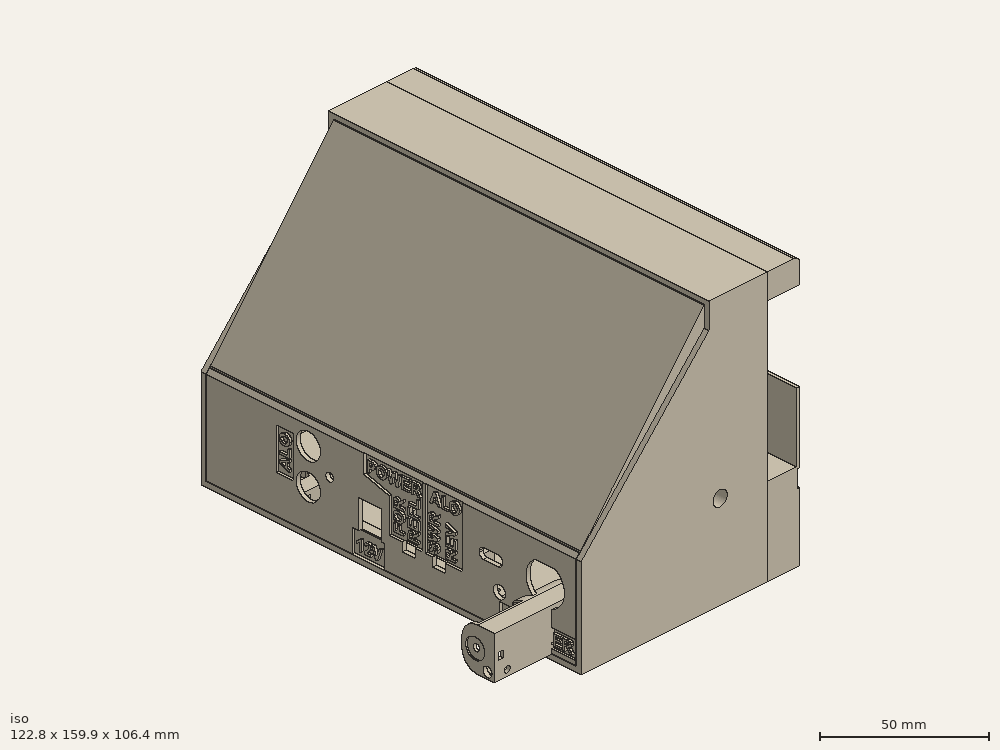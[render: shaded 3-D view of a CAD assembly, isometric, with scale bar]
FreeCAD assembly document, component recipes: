
FREECAD ASSEMBLY — COMPONENT RECIPES ("console")

This assembly document has 6 components, labeled P0..P5 below (a component is one placed body or linked part). 5 of them carry a construction recipe — the FreeCAD feature program that regenerates the part from scratch, quoted from this document or its linked companion documents; the rest are supplied as boundary geometry only. No exploded tour is included for this assembly.
NOTE — this tour is split across 2 documents so each fits a 32k-token context. This is document 1: the component sections continue in the remaining 1 document, each repeating the header above.
COMPONENT P0 — geometry summary ("AA single002"; no construction recipe available for this part):
  bounding box: 122.8 x 16.9 x 13.9 mm
  tessellated surface: 93,791 triangles
  volume: 2869 mm^3 (10% of its bounding box)
COMPONENT P1 — recipe-attached ("Cliff FC684204", modeled in this document).
Construction recipe (the document's own serialized feature program — sketch geometry with constraints, then the solid features built on it; lengths are millimeters unless a unit is written):

FEATURE [PartDesign::SubShapeBinder] Binder
  BindCopyOnChange = 0
  BindMode = 0
  ClaimChildren = false
  Context = -> Part [Body.Binder.]
  Fuse = false
  MakeFace = true
  OffsetFill = false
  OffsetIntersection = false
  OffsetJoinType = 0
  OffsetOpenResult = false
  PartialLoad = false
  Refine = true
  Relative = true
  Support = -> [<external console-placement.FCStd>#Assembly[meter.,meter001.,_M_pot.,_00DP6R7BLKM3QEBLK003.]]
  _Version = 2
FEATURE [PartDesign::SubShapeBinder] Binder001
  BindCopyOnChange = 0
  BindMode = 0
  ClaimChildren = false
  Context = -> Part [Body.Binder001.]
  Fuse = false
  MakeFace = true
  OffsetFill = false
  OffsetIntersection = false
  OffsetJoinType = 0
  OffsetOpenResult = false
  PartialLoad = false
  Refine = true
  Relative = true
  Support = -> [<external console-placement.FCStd>#Assembly[PCB_Assembly.pcb_imported.]]
  _Version = 2
FEATURE [PartDesign::Plane] DatumPlane  label="meter back"
  AttachmentSupport = -> [Binder]
  Length = 190.224
  MapMode = 5
  Placement = pos=(76.55,0,0) rot=(0.57735,-0.57735,-0.57735;2.0944rad)
  ResizeMode = 0
  Width = 149.914
FEATURE [Sketcher::SketchObject] Sketch
  ArcFitTolerance = 1e-06
  AttachmentSupport = -> [Binder]
  ExternalGeometry = -> [Binder,Binder001]
  FullyConstrained = true
  MakeInternals = false
  MapMode = 5
  Placement = pos=(76.55,0,0) rot=(0.57735,-0.57735,-0.57735;2.0944rad)
  sketch-geometry (17):
    g0: LineSegment StartX=-137.1 StartY=86.63 StartZ=0 EndX=-137.1 EndY=-7.62 EndZ=0
    g1: LineSegment StartX=-137.1 StartY=-7.62 StartZ=0 EndX=22.8 EndY=-7.62 EndZ=0
    g2: LineSegment StartX=22.8 StartY=-7.62 StartZ=0 EndX=22.8 EndY=86.63 EndZ=0
    g3: LineSegment [constr] StartX=22.8 StartY=86.63 StartZ=0 EndX=-137.1 EndY=86.63 EndZ=0
    g4: Circle CenterX=-125.984 CenterY=80.264 CenterZ=0 NormalX=0 NormalY=0 NormalZ=1 AngleXU=0 Radius=1.905
    g5: Circle CenterX=-77.216 CenterY=80.264 CenterZ=0 NormalX=0 NormalY=0 NormalZ=1 AngleXU=0 Radius=1.905
    g6: Circle CenterX=-125.984 CenterY=31.496 CenterZ=0 NormalX=0 NormalY=0 NormalZ=1 AngleXU=0 Radius=1.905
    g7: Circle CenterX=-77.216 CenterY=31.496 CenterZ=0 NormalX=0 NormalY=0 NormalZ=1 AngleXU=0 Radius=1.905
    g8: Circle CenterX=-101.6 CenterY=55.88 CenterZ=0 NormalX=0 NormalY=0 NormalZ=1 AngleXU=0 Radius=27.178
    g9: Circle CenterX=-12.7 CenterY=55.88 CenterZ=0 NormalX=0 NormalY=0 NormalZ=1 AngleXU=0 Radius=27.178
    g10: Circle CenterX=-37.084 CenterY=31.496 CenterZ=0 NormalX=0 NormalY=0 NormalZ=1 AngleXU=0 Radius=1.905
    g11: Circle CenterX=11.684 CenterY=31.496 CenterZ=0 NormalX=0 NormalY=0 NormalZ=1 AngleXU=0 Radius=1.905
    g12: Circle CenterX=11.684 CenterY=80.264 CenterZ=0 NormalX=0 NormalY=0 NormalZ=1 AngleXU=0 Radius=1.905
    g13: Circle CenterX=-37.084 CenterY=80.264 CenterZ=0 NormalX=0 NormalY=0 NormalZ=1 AngleXU=0 Radius=1.905
    g14: LineSegment StartX=-137.1 StartY=86.63 StartZ=0 EndX=-137.1 EndY=96.79 EndZ=0
    g15: LineSegment StartX=-137.1 StartY=96.79 StartZ=0 EndX=22.8 EndY=96.79 EndZ=0
    g16: LineSegment StartX=22.8 StartY=96.79 StartZ=0 EndX=22.8 EndY=86.63 EndZ=0
  constraints (38):
    c: Coincident(g0,g1)
    c: Coincident(g1,g2)
    c: Coincident(g2,g3)
    c: Coincident(g3,g0)
    c: Vertical(g0)
    c: Vertical(g2)
    c: Horizontal(g1)
    c: Coincident(g0,g-4)
    c: Coincident(g-3,g2)
    c: PointOnObject(g-18,g1)
    c: Coincident(g4,g-11)
    c: Coincident(g5,g-9)
    c: Coincident(g6,g-12)
    c: Coincident(g7,g-10)
    c: Coincident(g8,g-8)
    c: Coincident(g9,g-7)
    c: Coincident(g10,g-13)
    c: Coincident(g11,g-16)
    c: Coincident(g12,g-15)
    c: Coincident(g13,g-14)
    c: Equal(g4,g5)
    c: Equal(g4,g6)
    c: Equal(g4,g7)
    c: Equal(g4,g13)
    c: Equal(g4,g12)
    c: Equal(g4,g10)
    c: Equal(g4,g11)
    c: Equal(g8,g9)
    c: Diameter(g8) = 54.356
    c: Diameter(g4) = 3.81
    c: Coincident(g14,g0)
    c: Vertical(g14)
    c: Coincident(g15,g14)
    c: Horizontal(g15)
    c: Coincident(g16,g15)
    c: Coincident(g16,g2)
    c: Vertical(g16)
    c: DistanceY(g2,g15) = 10.16
FEATURE [PartDesign::Pad] Pad
  Direction = (-1,0,0)
  Length = 2.032
  Length2 = 10
  Profile = -> Sketch
  ReferenceAxis = -> Sketch [N_Axis]
  Refine = true
  Suppressed = false
  Type = 0
FEATURE [Sketcher::SketchObject] Sketch001
  ArcFitTolerance = 1e-06
  AttachmentSupport = -> [DatumPlane]
  ExternalGeometry = -> [Pad]
  FullyConstrained = false
  MakeInternals = false
  MapMode = 5
  Placement = pos=(76.55,0,0) rot=(0.57735,-0.57735,-0.57735;2.0944rad)
  sketch-geometry (11):
    g0: LineSegment StartX=-137.1 StartY=96.79 StartZ=0 EndX=-137.1 EndY=-9.652 EndZ=0
    g1: LineSegment StartX=-137.1 StartY=-9.652 StartZ=0 EndX=22.8 EndY=-9.652 EndZ=0
    g2: LineSegment StartX=22.8 StartY=-9.652 StartZ=0 EndX=22.8 EndY=96.79 EndZ=0
    g3: LineSegment StartX=-135.068 StartY=94.758 StartZ=0 EndX=-135.068 EndY=-7.62 EndZ=0
    g4: LineSegment StartX=-135.068 StartY=-7.62 StartZ=0 EndX=20.768 EndY=-7.62 EndZ=0
    g5: LineSegment StartX=20.768 StartY=-7.62 StartZ=0 EndX=20.768 EndY=94.758 EndZ=0
    g6: LineSegment StartX=-137.1 StartY=96.79 StartZ=0 EndX=22.8 EndY=96.79 EndZ=0
    g7: LineSegment StartX=20.768 StartY=94.758 StartZ=0 EndX=-135.068 EndY=94.758 EndZ=0
    g8: LineSegment [constr] StartX=-57.15 StartY=94.758 StartZ=0 EndX=-57.15 EndY=96.79 EndZ=0
    g9: LineSegment [constr] StartX=-57.15 StartY=-7.62 StartZ=0 EndX=-57.15 EndY=-9.652 EndZ=0
    g10: LineSegment [constr] StartX=-135.068 StartY=46.1442 StartZ=0 EndX=-137.1 EndY=46.1442 EndZ=0
  constraints (29):
    c: Coincident(g0,g1)
    c: Coincident(g1,g2)
    c: Vertical(g0)
    c: Vertical(g2)
    c: Horizontal(g1)
    c: DistanceY(g1,g-3) = 2.032
    c: Coincident(g3,g4)
    c: Coincident(g4,g5)
    c: Vertical(g3)
    c: Vertical(g5)
    c: Horizontal(g4)
    c: PointOnObject(g-3,g4)
    c: Coincident(g2,g-4)
    c: Coincident(g0,g-4)
    c: Coincident(g6,g0)
    c: Coincident(g6,g2)
    c: Coincident(g7,g5)
    c: Coincident(g7,g3)
    c: Horizontal(g7)
    c: Symmetric(g7,g7,g8)
    c: Symmetric(g6,g6,g8)
    c: Vertical(g8)
    c: Symmetric(g4,g4,g9)
    c: Symmetric(g1,g1,g9)
    c: Equal(g9,g8)
    c: PointOnObject(g10,g3)
    c: PointOnObject(g10,g0)
    c: Horizontal(g10)
    c: Equal(g10,g8)
FEATURE [PartDesign::Pad] Pad001
  BaseFeature = -> Pad
  Direction = (-1,0,0)
  Length = 10
  Length2 = 10
  Profile = -> Sketch001
  ReferenceAxis = -> Sketch001 [N_Axis]
  Refine = true
  Suppressed = false
  Type = 3
  UpToFace = -> Binder001 [Face2]
FEATURE [PartDesign::Plane] DatumPlane001  label="console left"
  AttachmentSupport = -> [Binder]
  Length = 123.815
  MapMode = 5
  Placement = pos=(0,137.1,1.51e-14) rot=(0,0.707107,0.707107;3.14159rad)
  ResizeMode = 0
  Width = 144.055
FEATURE [Sketcher::SketchObject] Sketch002  label="angled back sketch"
  ArcFitTolerance = 1e-06
  AttachmentSupport = -> [DatumPlane001]
  ExternalGeometry = -> [Binder,Pad001]
  FullyConstrained = false
  MakeInternals = false
  MapMode = 5
  Placement = pos=(0,137.1,1.51e-14) rot=(0,0.707107,0.707107;3.14159rad)
  sketch-geometry (5):
    g0: LineSegment StartX=-52.039 StartY=86.63 StartZ=0 EndX=0 EndY=30.988 EndZ=0
    g1: LineSegment StartX=-52.039 StartY=86.63 StartZ=0 EndX=-52.039 EndY=104.011 EndZ=0
    g2: LineSegment StartX=-52.039 StartY=104.011 StartZ=0 EndX=12.4998 EndY=104.011 EndZ=0
    g3: LineSegment StartX=12.4998 StartY=104.011 StartZ=0 EndX=12.4998 EndY=30.988 EndZ=0
    g4: LineSegment StartX=12.4998 StartY=30.988 StartZ=0 EndX=0 EndY=30.988 EndZ=0
  constraints (13):
    c: PointOnObject(g0,g-3)
    c: Vertical(g0,g-5)
    c: DistanceY(g-5,g0) = 40.64
    c: PointOnObject(g0,g-4)
    c: Coincident(g1,g0)
    c: Vertical(g1)
    c: Coincident(g2,g1)
    c: Horizontal(g2)
    c: Coincident(g3,g2)
    c: Vertical(g3)
    c: Coincident(g4,g3)
    c: Coincident(g4,g0)
    c: Horizontal(g4)
FEATURE [PartDesign::Pocket] Pocket
  BaseFeature = -> Pad001
  Direction = (0,-1,2e-16)
  Length = 5
  Length2 = 5
  Profile = -> Sketch002
  ReferenceAxis = -> Sketch002 [N_Axis]
  Refine = true
  Suppressed = false
  Type = 1
FEATURE [PartDesign::SubShapeBinder] Binder003
  BindCopyOnChange = 0
  BindMode = 0
  ClaimChildren = false
  Context = -> Part [Body.Binder003.]
  Fuse = false
  MakeFace = true
  OffsetFill = false
  OffsetIntersection = false
  OffsetJoinType = 0
  OffsetOpenResult = false
  PartialLoad = false
  Refine = true
  Relative = true
  Support = -> [Link[PCB_Assembly.WP154A4SUREQBFZGC.,PCB_Assembly.WP154A4SUREQBFZGC001.,PCB_Assembly.WP154A4SUREQBFZGC002.,PCB_Assembly.WP154A4SUREQBFZGC003.,PCB_Assembly.WP154A4SUREQBFZGC004.,PCB_Assembly.WP154A4SUREQBFZGC005.,_M_pot.,_00DP6R7BLKM3QEBLK003.]]
  _Version = 2
FEATURE [Sketcher::SketchObject] Sketch025
  ArcFitTolerance = 1e-06
  AttachmentSupport = -> [DatumPlane]
  ExternalGeometry = -> [Binder]
  FullyConstrained = true
  MakeInternals = false
  MapMode = 5
  Placement = pos=(76.55,0,0) rot=(0.57735,-0.57735,-0.57735;2.0944rad)
  sketch-geometry (15):
    g0: Circle [constr] CenterX=-131.385 CenterY=91.075 CenterZ=0 NormalX=0 NormalY=0 NormalZ=1 AngleXU=0 Radius=3.683
    g1: Circle CenterX=-131.385 CenterY=91.075 CenterZ=0 NormalX=0 NormalY=0 NormalZ=1 AngleXU=0 Radius=1.524
    g2: Circle [constr] CenterX=17.085 CenterY=91.075 CenterZ=0 NormalX=0 NormalY=0 NormalZ=1 AngleXU=0 Radius=3.683
    g3: Circle CenterX=17.085 CenterY=91.075 CenterZ=0 NormalX=0 NormalY=0 NormalZ=1 AngleXU=0 Radius=1.524
    g4: Circle [constr] CenterX=-109.668 CenterY=-3.937 CenterZ=0 NormalX=0 NormalY=0 NormalZ=1 AngleXU=0 Radius=3.683
    g5: Circle [constr] CenterX=16.958 CenterY=-3.937 CenterZ=0 NormalX=0 NormalY=0 NormalZ=1 AngleXU=0 Radius=3.683
    g6: Circle CenterX=-109.668 CenterY=-3.937 CenterZ=0 NormalX=0 NormalY=0 NormalZ=1 AngleXU=0 Radius=1.524
    g7: Circle CenterX=16.958 CenterY=-3.937 CenterZ=0 NormalX=0 NormalY=0 NormalZ=1 AngleXU=0 Radius=1.524
    g8: LineSegment [constr] StartX=-66.1 StartY=86.63 StartZ=0 EndX=-48.2 EndY=25.13 EndZ=0
    g9: Circle CenterX=-57.15 CenterY=55.88 CenterZ=0 NormalX=0 NormalY=0 NormalZ=1 AngleXU=0 Radius=1.524
    g10: LineSegment StartX=-62.8269 StartY=92.98 StartZ=0 EndX=-62.8269 EndY=79.7415 EndZ=0
    g11: LineSegment StartX=-62.8269 StartY=79.7415 StartZ=0 EndX=-51.4731 EndY=79.7415 EndZ=0
    g12: LineSegment StartX=-51.4731 StartY=79.7415 StartZ=0 EndX=-51.4731 EndY=92.98 EndZ=0
    g13: LineSegment StartX=-51.4731 StartY=92.98 StartZ=0 EndX=-62.8269 EndY=92.98 EndZ=0
    g14: GeomPoint X=-57.15 Y=79.7415 Z=0
  constraints (37):
    c: Diameter(g0) = 7.366
    c: Tangent(g0,g-4)
    c: Tangent(g0,g-3)
    c: Coincident(g1,g0)
    c: Diameter(g1) = 3.048
    c: Equal(g2,g0)
    c: Tangent(g2,g-5)
    c: Tangent(g2,g-3)
    c: Coincident(g3,g2)
    c: Equal(g3,g1)
    c: Equal(g4,g5)
    c: Equal(g4,g0)
    c: Tangent(g4,g-6)
    c: Tangent(g5,g-6)
    c: DistanceX(g-6,g4) = 25.4
    c: DistanceX(g5,g-6) = 3.81
    c: Coincident(g6,g4)
    c: Coincident(g7,g5)
    c: Equal(g7,g6)
    c: Equal(g6,g1)
    c: Coincident(g8,g-7)
    c: Coincident(g8,g-8)
    c: Symmetric(g8,g8,g9)
    c: Equal(g9,g7)
    c: Coincident(g10,g11)
    c: Coincident(g11,g12)
    c: Coincident(g12,g13)
    c: Coincident(g13,g10)
    c: Vertical(g10)
    c: Vertical(g12)
    c: Horizontal(g11)
    c: Horizontal(g13)
    c: Symmetric(g11,g10,g14)
    c: Vertical(g9,g14)
    c: DistanceX(g10,g12) = 11.3538
    c: DistanceY(g11,g12) = 13.2385
    c: DistanceY(g12,g-5) = 1.778
FEATURE [PartDesign::Pocket] Pocket009  label="screw holes to front panel"
  BaseFeature = -> Pocket
  Direction = (1,0,0)
  Length = 5.00126
  Length2 = 5
  Profile = -> Sketch025
  ReferenceAxis = -> Sketch025 [N_Axis]
  Refine = true
  Reversed = true
  Suppressed = false
  Type = 1
FEATURE [PartDesign::Plane] DatumPlane004  label="normal to sloped lid"
  AttachmentSupport = -> [Pocket009]
  Length = 194.066
  MapMode = 7
  Placement = pos=(52.039,-20.768,86.63) rot=(0.344679,0.344679,0.873151;1.70603rad)
  ResizeMode = 0
  Width = 189.332
FEATURE [Sketcher::SketchObject] Sketch027
  ArcFitTolerance = 1e-06
  AttachmentSupport = -> [DatumPlane004]
  ExternalGeometry = -> [Pocket009]
  FullyConstrained = true
  MakeInternals = false
  MapMode = 5
  Placement = pos=(52.039,-20.768,86.63) rot=(0.344679,0.344679,0.873151;1.70603rad)
  sketch-geometry (6):
    g0: LineSegment StartX=0 StartY=-4.318 StartZ=0 EndX=2.54 EndY=-1.778 EndZ=0
    g1: LineSegment StartX=2.54 StartY=-1.778 StartZ=0 EndX=0 EndY=-1.778 EndZ=0
    g2: LineSegment StartX=0 StartY=-1.778 StartZ=0 EndX=0 EndY=-4.318 EndZ=0
    g3: LineSegment StartX=153.296 StartY=-1.778 StartZ=0 EndX=155.836 EndY=-1.778 EndZ=0
    g4: LineSegment StartX=155.836 StartY=-1.778 StartZ=0 EndX=155.836 EndY=-4.318 EndZ=0
    g5: LineSegment StartX=155.836 StartY=-4.318 StartZ=0 EndX=153.296 EndY=-1.778 EndZ=0
  constraints (18):
    c: Coincident(g1,g0)
    c: PointOnObject(g1,g-2)
    c: Horizontal(g1)
    c: Coincident(g2,g1)
    c: Vertical(g2)
    c: Coincident(g0,g2)
    c: DistanceY(g1,g-1) = 1.778
    c: Distance(g1,g1) = 2.54
    c: Angle(g0,g2) = 0.785398
    c: Horizontal(g3)
    c: Coincident(g4,g3)
    c: Vertical(g4)
    c: Coincident(g5,g4)
    c: Coincident(g5,g3)
    c: Vertical(g3,g-3)
    c: Horizontal(g3,g0)
    c: Equal(g1,g3)
    c: Equal(g5,g0)
FEATURE [PartDesign::Pad] Pad006  label="lid shelf"
  BaseFeature = -> Pocket009
  Direction = (0.683065,0,0.730358)
  Length = 10
  Length2 = 10
  Profile = -> Sketch027
  ReferenceAxis = -> Sketch027 [N_Axis]
  Refine = true
  Reversed = true
  Suppressed = false
  Type = 3
  UpToFace = -> Pocket009 [Face32]
FEATURE [PartDesign::Plane] DatumPlane005  label="PCB back"
  AttachmentSupport = -> [Binder001]
  Length = 190.224
  MapMode = 5
  Placement = pos=(0,0,0) rot=(0.57735,-0.57735,-0.57735;2.0944rad)
  ResizeMode = 0
  Width = 149.914
FEATURE [Sketcher::SketchObject] Sketch028
  ArcFitTolerance = 1e-06
  AttachmentSupport = -> [DatumPlane005]
  ExternalGeometry = -> [Pad006,DatumPlane001]
  FullyConstrained = false
  MakeInternals = false
  MapMode = 5
  Placement = pos=(0,0,0) rot=(0.57735,-0.57735,-0.57735;2.0944rad)
  sketch-geometry (8):
    g0: LineSegment StartX=-137.1 StartY=-9.652 StartZ=0 EndX=22.8 EndY=-9.652 EndZ=0
    g1: LineSegment StartX=22.8 StartY=-9.652 StartZ=0 EndX=22.8 EndY=30.988 EndZ=0
    g2: LineSegment StartX=22.8 StartY=30.988 StartZ=0 EndX=20.768 EndY=30.988 EndZ=0
    g3: LineSegment StartX=20.768 StartY=30.988 StartZ=0 EndX=20.768 EndY=-7.62 EndZ=0
    g4: LineSegment StartX=20.768 StartY=-7.62 StartZ=0 EndX=-135.068 EndY=-7.62 EndZ=0
    g5: LineSegment StartX=-135.068 StartY=-7.62 StartZ=0 EndX=-135.068 EndY=30.988 EndZ=0
    g6: LineSegment StartX=-137.1 StartY=30.988 StartZ=0 EndX=-137.1 EndY=-9.652 EndZ=0
    g7: LineSegment StartX=-135.068 StartY=30.988 StartZ=0 EndX=-137.1 EndY=30.988 EndZ=0
  constraints (14):
    c: Coincident(g0,g-4)
    c: Coincident(g1,g0)
    c: Coincident(g1,g-3)
    c: Coincident(g2,g1)
    c: Coincident(g2,g-6)
    c: Coincident(g3,g2)
    c: Coincident(g3,g-5)
    c: Coincident(g4,g3)
    c: Coincident(g4,g-5)
    c: Coincident(g5,g4)
    c: Coincident(g5,g-8)
    c: Coincident(g7,g5)
    c: Coincident(g7,g6)
    c: Horizontal(g7)
FEATURE [PartDesign::Pad] Pad007  label="extend back"
  BaseFeature = -> Pad006
  Direction = (-1,0,0)
  Length = 1.651
  Length2 = 10
  Profile = -> Sketch028
  ReferenceAxis = -> Sketch028 [N_Axis]
  Refine = true
  Suppressed = false
  Type = 0
FEATURE [PartDesign::Plane] DatumPlane006  label="sub panel bottom"
  AttachmentSupport = -> [Pad006]
  Length = 127.233
  MapMode = 5
  Placement = pos=(0,0,-9.652) rot=(1,0,0;3.14159rad)
  ResizeMode = 0
  Width = 187.783
FEATURE [Sketcher::SketchObject] Sketch029
  ArcFitTolerance = 1e-06
  AttachmentSupport = -> [DatumPlane006]
  ExternalGeometry = -> [Pad006]
  FullyConstrained = true
  MakeInternals = false
  MapMode = 5
  Placement = pos=(0,0,-9.652) rot=(1,0,0;3.14159rad)
  sketch-geometry (6):
    g0: LineSegment StartX=0 StartY=20.768 StartZ=0 EndX=0 EndY=18.228 EndZ=0
    g1: LineSegment StartX=0 StartY=18.228 StartZ=0 EndX=3.81 EndY=20.768 EndZ=0
    g2: LineSegment StartX=3.81 StartY=20.768 StartZ=0 EndX=0 EndY=20.768 EndZ=0
    g3: LineSegment StartX=0 StartY=-135.068 StartZ=0 EndX=0 EndY=-132.528 EndZ=0
    g4: LineSegment StartX=0 StartY=-135.068 StartZ=0 EndX=3.81 EndY=-135.068 EndZ=0
    g5: LineSegment StartX=3.81 StartY=-135.068 StartZ=0 EndX=0 EndY=-132.528 EndZ=0
  constraints (15):
    c: Coincident(g0,g-4)
    c: Coincident(g0,g-7)
    c: Coincident(g1,g0)
    c: Coincident(g2,g1)
    c: Coincident(g2,g0)
    c: Coincident(g3,g-5)
    c: Vertical(g3)
    c: Equal(g3,g0)
    c: Horizontal(g2)
    c: DistanceX(g0,g1) = 3.81
    c: Coincident(g4,g3)
    c: Coincident(g5,g4)
    c: Coincident(g5,g3)
    c: Horizontal(g4)
    c: Equal(g5,g1)
FEATURE [PartDesign::Pad] Pad008
  BaseFeature = -> Pad007
  Direction = (0,0,-1)
  Length = 27.94
  Length2 = 10
  Profile = -> Sketch029
  ReferenceAxis = -> Sketch029 [N_Axis]
  Refine = true
  Reversed = true
  Suppressed = false
  Type = 3
  UpToFace = -> Pad007 [Face37]
FEATURE [Sketcher::SketchObject] Sketch030
  ArcFitTolerance = 1e-06
  AttachmentSupport = -> [DatumPlane001]
  ExternalGeometry = -> [Pad008]
  FullyConstrained = true
  MakeInternals = false
  MapMode = 5
  Placement = pos=(0,137.1,1.51e-14) rot=(0,0.707107,0.707107;3.14159rad)
  sketch-geometry (3):
    g0: LineSegment StartX=-3.04e-14 StartY=-7.62 StartZ=0 EndX=-3.04e-14 EndY=-6.35 EndZ=0
    g1: LineSegment StartX=-3.04e-14 StartY=-6.35 StartZ=0 EndX=-1.27 EndY=-7.62 EndZ=0
    g2: LineSegment StartX=-1.27 StartY=-7.62 StartZ=0 EndX=-3.04e-14 EndY=-7.62 EndZ=0
  constraints (8):
    c: Coincident(g0,g-3)
    c: Coincident(g1,g0)
    c: Coincident(g2,g1)
    c: Coincident(g2,g0)
    c: Horizontal(g2)
    c: Vertical(g0)
    c: Angle(g2,g1) = 0.785398
    c: DistanceY(g0,g0) = 1.27
FEATURE [PartDesign::Pad] Pad009  label="back panel block"
  BaseFeature = -> Pad008
  Direction = (0,1,-2e-16)
  Length = 10
  Length2 = 10
  Profile = -> Sketch030
  ReferenceAxis = -> Sketch030 [N_Axis]
  Refine = true
  Suppressed = false
  Type = 3
  UpToFace = -> Pad008 [Face27]
FEATURE [PartDesign::Plane] DatumPlane011  label="PCB left (gapped)"
  AttachmentOffset = pos=(0,0,2.54) rot=(0,0,1;0rad)
  AttachmentSupport = -> [Binder001]
  Length = 123.815
  MapMode = 5
  Placement = pos=(0,104.14,-6e-16) rot=(0,0.707107,0.707107;3.14159rad)
  ResizeMode = 0
  Width = 144.055
FEATURE [PartDesign::Plane] DatumPlane012  label="PCB right (gapped)"
  AttachmentOffset = pos=(0,0,2.54) rot=(0,0,1;0rad)
  AttachmentSupport = -> [Binder001]
  Length = 123.815
  MapMode = 5
  Placement = pos=(0,-2.54,6e-16) rot=(1,0,0;1.5708rad)
  ResizeMode = 0
  Width = 144.055
FEATURE [Sketcher::SketchObject] Sketch038
  ArcFitTolerance = 1e-06
  AttachmentSupport = -> [DatumPlane011]
  ExternalGeometry = -> [Pad009]
  FullyConstrained = true
  MakeInternals = false
  MapMode = 5
  Placement = pos=(0,104.14,-6e-16) rot=(0,0.707107,0.707107;3.14159rad)
  sketch-geometry (4):
    g0: LineSegment StartX=-21.971 StartY=-9.652 StartZ=0 EndX=-17.399 EndY=-5.08 EndZ=0
    g1: LineSegment StartX=-17.399 StartY=-5.08 StartZ=0 EndX=-4.699 EndY=-5.08 EndZ=0
    g2: LineSegment StartX=-4.699 StartY=-5.08 StartZ=0 EndX=-4.699 EndY=-9.652 EndZ=0
    g3: LineSegment StartX=-4.699 StartY=-9.652 StartZ=0 EndX=-21.971 EndY=-9.652 EndZ=0
  constraints (12):
    c: PointOnObject(g0,g-3)
    c: Coincident(g1,g0)
    c: Horizontal(g1)
    c: Coincident(g2,g1)
    c: PointOnObject(g2,g-3)
    c: Vertical(g2)
    c: Coincident(g3,g2)
    c: Coincident(g3,g0)
    c: Angle(g3,g0) = 0.785398
    c: Distance(g2,g1) = 4.572
    c: DistanceX(g2,g-3) = 6.35
    c: DistanceX(g0,g1) = 12.7
FEATURE [PartDesign::Pad] Pad014  label="bottom boss"
  BaseFeature = -> Pad009
  Direction = (0,1,-2e-16)
  Length = 12.7
  Length2 = 10
  Profile = -> Sketch038
  ReferenceAxis = -> Sketch038 [N_Axis]
  Refine = true
  Suppressed = false
  Type = 0
FEATURE [Sketcher::SketchObject] Sketch039
  ArcFitTolerance = 1e-06
  AttachmentSupport = -> [DatumPlane012]
  ExternalGeometry = -> [Pad014]
  FullyConstrained = true
  MakeInternals = false
  MapMode = 5
  Placement = pos=(0,-2.54,6e-16) rot=(1,0,0;1.5708rad)
  sketch-geometry (4):
    g0: LineSegment StartX=4.699 StartY=-5.08 StartZ=0 EndX=17.399 EndY=-5.08 EndZ=0
    g1: LineSegment StartX=17.399 StartY=-5.08 StartZ=0 EndX=21.971 EndY=-9.652 EndZ=0
    g2: LineSegment StartX=21.971 StartY=-9.652 StartZ=0 EndX=4.699 EndY=-9.652 EndZ=0
    g3: LineSegment StartX=4.699 StartY=-9.652 StartZ=0 EndX=4.699 EndY=-5.08 EndZ=0
  constraints (10):
    c: Coincident(g0,g-4)
    c: Coincident(g0,g-5)
    c: Coincident(g1,g0)
    c: PointOnObject(g1,g-3)
    c: Coincident(g2,g1)
    c: PointOnObject(g2,g-3)
    c: Coincident(g3,g2)
    c: Coincident(g3,g0)
    c: Vertical(g3)
    c: PointOnObject(g-5,g1)
FEATURE [PartDesign::Pad] Pad015  label="bottom boss 2"
  BaseFeature = -> Pad014
  Direction = (0,-1,2e-16)
  Length = 12.7
  Length2 = 10
  Profile = -> Sketch039
  ReferenceAxis = -> Sketch039 [N_Axis]
  Refine = true
  Suppressed = false
  Type = 0
FEATURE [PartDesign::Plane] DatumPlane013  label="interface to back panel"
  AttachmentSupport = -> [Pad015]
  Length = 127.233
  MapMode = 5
  Placement = pos=(0,-1.1e-15,-5.08) rot=(0,0,1;0rad)
  ResizeMode = 0
  Width = 187.783
FEATURE [Sketcher::SketchObject] Sketch040
  ArcFitTolerance = 1e-06
  AttachmentSupport = -> [DatumPlane013]
  ExternalGeometry = -> [Pad015]
  FullyConstrained = true
  MakeInternals = false
  MapMode = 5
  Placement = pos=(0,-1.1e-15,-5.08) rot=(0,0,1;0rad)
  sketch-geometry (4):
    g0: LineSegment [constr] StartX=17.399 StartY=-15.24 StartZ=0 EndX=4.699 EndY=-2.54 EndZ=0
    g1: LineSegment [constr] StartX=17.399 StartY=104.14 StartZ=0 EndX=4.699 EndY=116.84 EndZ=0
    g2: Circle CenterX=11.049 CenterY=110.49 CenterZ=0 NormalX=0 NormalY=0 NormalZ=1 AngleXU=0 Radius=1.905
    g3: Circle CenterX=11.049 CenterY=-8.89 CenterZ=0 NormalX=0 NormalY=0 NormalZ=1 AngleXU=0 Radius=1.905
  constraints (8):
    c: Coincident(g0,g-5)
    c: Coincident(g0,g-6)
    c: Coincident(g1,g-3)
    c: Coincident(g1,g-4)
    c: Symmetric(g1,g1,g2)
    c: Symmetric(g0,g0,g3)
    c: Equal(g3,g2)
    c: Diameter(g2) = 3.81
FEATURE [PartDesign::Pocket] Pocket012  label="screw holes in bosses"
  BaseFeature = -> Pad015
  Direction = (0,0,-1)
  Length = 5
  Length2 = 5
  Profile = -> Sketch040
  ReferenceAxis = -> Sketch040 [N_Axis]
  Refine = true
  Suppressed = false
  Type = 1
FEATURE [Sketcher::SketchObject] Sketch041
  ArcFitTolerance = 1e-06
  AttachmentSupport = -> [Pocket012]
  ExternalGeometry = -> [Pocket012]
  FullyConstrained = true
  MakeInternals = false
  MapMode = 5
  Placement = pos=(0,0,-9.652) rot=(1,0,0;3.14159rad)
  sketch-geometry (2):
    g0: Circle CenterX=11.049 CenterY=-110.49 CenterZ=0 NormalX=0 NormalY=0 NormalZ=1 AngleXU=0 Radius=3.556
    g1: Circle CenterX=11.049 CenterY=8.89 CenterZ=0 NormalX=0 NormalY=0 NormalZ=1 AngleXU=0 Radius=3.556
  constraints (4):
    c: Coincident(g0,g-4)
    c: Diameter(g0) = 7.112
    c: Coincident(g1,g-3)
    c: Equal(g1,g0)
FEATURE [PartDesign::Pocket] Pocket013  label="countersink at bottom"
  BaseFeature = -> Pocket012
  Direction = (0,0,1)
  Length = 2.54
  Length2 = 5
  Profile = -> Sketch041
  ReferenceAxis = -> Sketch041 [N_Axis]
  Refine = true
  Suppressed = false
  Type = 0
FEATURE [PartDesign::Plane] DatumPlane016  label="console pivot boss"
  AttachmentOffset = pos=(0,0,-36.83) rot=(0,0,1;0rad)
  AttachmentSupport = -> [DatumPlane006]
  Length = 127.233
  MapMode = 5
  Placement = pos=(0,0,27.178) rot=(1,0,0;3.14159rad)
  ResizeMode = 0
  Width = 187.783
FEATURE [Sketcher::SketchObject] Sketch045
  ArcFitTolerance = 1e-06
  AttachmentSupport = -> [DatumPlane016]
  ExternalGeometry = -> [Pocket013]
  FullyConstrained = true
  MakeInternals = false
  MapMode = 5
  Placement = pos=(0,0,27.178) rot=(1,0,0;3.14159rad)
  sketch-geometry (8):
    g0: LineSegment StartX=49.118 StartY=20.768 StartZ=0 EndX=71.978 EndY=20.768 EndZ=0
    g1: LineSegment StartX=71.978 StartY=20.768 StartZ=0 EndX=64.358 EndY=13.148 EndZ=0
    g2: LineSegment StartX=64.358 StartY=13.148 StartZ=0 EndX=49.118 EndY=13.148 EndZ=0
    g3: LineSegment StartX=49.118 StartY=13.148 StartZ=0 EndX=49.118 EndY=20.768 EndZ=0
    g4: LineSegment StartX=49.118 StartY=-127.448 StartZ=0 EndX=64.358 EndY=-127.448 EndZ=0
    g5: LineSegment StartX=64.358 StartY=-127.448 StartZ=0 EndX=71.978 EndY=-135.068 EndZ=0
    g6: LineSegment StartX=71.978 StartY=-135.068 StartZ=0 EndX=49.118 EndY=-135.068 EndZ=0
    g7: LineSegment StartX=49.118 StartY=-135.068 StartZ=0 EndX=49.118 EndY=-127.448 EndZ=0
  constraints (22):
    c: Coincident(g3,g0)
    c: Coincident(g3,g2)
    c: Coincident(g2,g1)
    c: Coincident(g1,g0)
    c: Tangent(g0,g-3)
    c: Angle(g0,g1) = 0.785398
    c: Perpendicular(g2,g3)
    c: Parallel(g0,g2)
    c: DistanceY(g2,g0) = 7.62
    c: DistanceX(g2,g1) = 15.24
    c: DistanceX(g0,g-3) = 2.54
    c: Coincident(g4,g5)
    c: Coincident(g7,g4)
    c: Coincident(g6,g7)
    c: Coincident(g6,g5)
    c: Tangent(g-4,g6)
    c: Perpendicular(g7,g4)
    c: Perpendicular(g6,g7)
    c: Vertical(g0,g5)
    c: Equal(g4,g2)
    c: Equal(g3,g7)
    c: Equal(g5,g1)
FEATURE [PartDesign::Pad] Pad017  label="pivot mounting bosses"
  BaseFeature = -> Pocket013
  Direction = (0,0,-1)
  Length = 15.24
  Length2 = 10
  Midplane = true
  Profile = -> Sketch045
  ReferenceAxis = -> Sketch045 [N_Axis]
  Refine = true
  Suppressed = false
  Type = 0
FEATURE [Sketcher::SketchObject] Sketch046
  ArcFitTolerance = 1e-06
  AttachmentSupport = -> [DatumPlane017]
  ExternalGeometry = -> [Pad017]
  FullyConstrained = true
  MakeInternals = false
  MapMode = 5
  Placement = pos=(0,127.448,0) rot=(1,0,0;1.5708rad)
  sketch-geometry (2):
    g0: LineSegment [constr] StartX=64.358 StartY=19.558 StartZ=0 EndX=49.118 EndY=34.798 EndZ=0
    g1: Circle CenterX=56.738 CenterY=27.178 CenterZ=0 NormalX=0 NormalY=0 NormalZ=1 AngleXU=0 Radius=2.9718
  constraints (4):
    c: Coincident(g0,g-4)
    c: Coincident(g-3,g0)
    c: Symmetric(g0,g0,g1)
    c: Diameter(g1) = 5.9436
FEATURE [PartDesign::Plane] DatumPlane035  label="Front of sub panel"
  AttachmentSupport = -> [Pad001]
  Length = 190.224
  MapMode = 5
  Placement = pos=(76.55,0,0) rot=(0.57735,0.57735,0.57735;2.0944rad)
  ResizeMode = 0
  Width = 149.914
FEATURE [PartDesign::ShapeBinder] ReferencePocket019
  Support = -> [Pocket019]
  TraceSupport = false
FEATURE [PartDesign::Plane] DatumPlane051
  AttachmentSupport = -> [ReferencePocket019]
  Length = 143.545
  MapMode = 5
  Placement = pos=(76.55,0,0) rot=(0.57735,0.57735,0.57735;2.0944rad)
  ResizeMode = 0
  Width = 66.0169
FEATURE [Sketcher::SketchObject] Sketch117
  ArcFitTolerance = 1e-06
  AttachmentSupport = -> [DatumPlane051]
  FullyConstrained = false
  MakeInternals = false
  MapMode = 5
  Placement = pos=(76.55,0,0) rot=(0.57735,0.57735,0.57735;2.0944rad)
  sketch-geometry (4):
    g0: LineSegment StartX=-92.3243 StartY=148.614 StartZ=0 EndX=-92.3243 EndY=-55.6635 EndZ=0
    g1: LineSegment StartX=-92.3243 StartY=-55.6635 StartZ=0 EndX=191.258 EndY=-55.6635 EndZ=0
    g2: LineSegment StartX=191.258 StartY=-55.6635 StartZ=0 EndX=191.258 EndY=148.614 EndZ=0
    g3: LineSegment StartX=191.258 StartY=148.614 StartZ=0 EndX=-92.3243 EndY=148.614 EndZ=0
  constraints (8):
    c: Coincident(g0,g1)
    c: Coincident(g1,g2)
    c: Coincident(g2,g3)
    c: Coincident(g3,g0)
    c: Vertical(g0)
    c: Vertical(g2)
    c: Horizontal(g1)
    c: Horizontal(g3)
FEATURE [PartDesign::SubShapeBinder] Binder019
  BindCopyOnChange = 0
  BindMode = 0
  ClaimChildren = false
  Context = -> Part [Body007.Binder019.]
  Fuse = false
  MakeFace = true
  OffsetFill = false
  OffsetIntersection = false
  OffsetJoinType = 0
  OffsetOpenResult = false
  PartialLoad = false
  Refine = true
  Relative = true
  Support = -> [Body]
  _Version = 2
FEATURE [PartDesign::Plane] DatumPlane058
  AttachmentSupport = -> [Pocket019]
  Length = 256.637
  MapMode = 5
  Placement = pos=(76.55,0,0) rot=(0.57735,0.57735,0.57735;2.0944rad)
  ResizeMode = 0
  Width = 207.153
FEATURE [Sketcher::SketchObject] Sketch133
  ArcFitTolerance = 1e-06
  AttachmentSupport = -> [DatumPlane058]
  FullyConstrained = false
  MakeInternals = false
  MapMode = 5
  Placement = pos=(76.55,0,0) rot=(0.57735,0.57735,0.57735;2.0944rad)
  sketch-geometry (4):
    g0: LineSegment StartX=-44.3306 StartY=119.029 StartZ=0 EndX=-44.3306 EndY=-49.7398 EndZ=0
    g1: LineSegment StartX=-44.3306 StartY=-49.7398 StartZ=0 EndX=173.922 EndY=-49.7398 EndZ=0
    g2: LineSegment StartX=173.922 StartY=-49.7398 StartZ=0 EndX=173.922 EndY=119.029 EndZ=0
    g3: LineSegment StartX=173.922 StartY=119.029 StartZ=0 EndX=-44.3306 EndY=119.029 EndZ=0
  constraints (8):
    c: Coincident(g0,g1)
    c: Coincident(g1,g2)
    c: Coincident(g2,g3)
    c: Coincident(g3,g0)
    c: Vertical(g0)
    c: Vertical(g2)
    c: Horizontal(g1)
    c: Horizontal(g3)
FEATURE [PartDesign::Pad] Pad038
  Direction = (1,0,0)
  Length = 50.8
  Length2 = 10
  Placement = pos=(76.55,0,0) rot=(0.57735,0.57735,0.57735;2.0944rad)
  Profile = -> Sketch133
  ReferenceAxis = -> Sketch133 [N_Axis]
  Refine = true
  Suppressed = false
  Type = 0
FEATURE [PartDesign::Body] Body007  label="front clipper"
  AllowCompound = false
  Group = -> [Binder019,DatumPlane058,Sketch133,Pad038]
  Origin = -> Origin013
  Tip = -> Pad038
FEATURE [PartDesign::Body] Body  label="sub panel body"
  AllowCompound = false
  Group = -> [Binder,Binder001,DatumPlane,Sketch,Pad,Sketch001,Pad001,DatumPlane001,Sketch002,DatumPlane035,Pocket,Binder003,Sketch025,Pocket009,DatumPlane004,DatumPlane005,DatumPlane006,Sketch027,DatumPlane016,Pad006,Sketch028,Pad007,Sketch029,Pad008,Sketch030,Pad009,DatumPlane011,DatumPlane012,Sketch038,Pad014,Sketch039,Pad015,DatumPlane013,Sketch040,Pocket012,Sketch041,Pocket013,Sketch045,Pad017,Sketch046,+28 more]
  Origin = -> Origin001
  Tip = -> Pocket042
FEATURE [PartDesign::FeatureBase] Clone
  BaseFeature = -> Body004
  Suppressed = false
FEATURE [PartDesign::Body] Body005  label="light pipe sub panel"
  AllowCompound = false
  Group = -> [Clone,ReferencePocket019,DatumPlane051,Sketch117]
  Origin = -> Origin011
  Tip = -> Clone
COMPONENT P2 — recipe-attached ("front panel", modeled in this document).
Construction recipe (the document's own serialized feature program — sketch geometry with constraints, then the solid features built on it; lengths are millimeters unless a unit is written):

FEATURE [PartDesign::SubShapeBinder] Binder004
  BindCopyOnChange = 0
  BindMode = 0
  ClaimChildren = false
  Context = -> Part001 [Body001.Binder004.]
  Fuse = false
  MakeFace = true
  OffsetFill = false
  OffsetIntersection = false
  OffsetJoinType = 0
  OffsetOpenResult = false
  PartialLoad = false
  Refine = true
  Relative = true
  Support = -> [Part]
  _Version = 2
FEATURE [PartDesign::SubShapeBinder] Binder005
  BindCopyOnChange = 0
  BindMode = 0
  ClaimChildren = false
  Context = -> Part001 [Body001.Binder005.]
  Fuse = false
  MakeFace = true
  OffsetFill = false
  OffsetIntersection = false
  OffsetJoinType = 0
  OffsetOpenResult = false
  PartialLoad = false
  Refine = true
  Relative = true
  Support = -> [Link[_M_pot.,_00DP6R7BLKM3QEBLK003.]]
  _Version = 2
FEATURE [PartDesign::Plane] DatumPlane002  label="pot panel inside"
  AttachmentSupport = -> [Binder005]
  Length = 150.095
  MapMode = 11
  Placement = pos=(88.5499,-6.858,7.62) rot=(0.707107,0,0.707107;3.14159rad)
  ResizeMode = 0
  Width = 192.491
FEATURE [PartDesign::SubShapeBinder] Binder006
  BindCopyOnChange = 0
  BindMode = 0
  ClaimChildren = false
  Context = -> Part001 [Body001.Binder006.]
  Fuse = false
  MakeFace = true
  OffsetFill = false
  OffsetIntersection = false
  OffsetJoinType = 0
  OffsetOpenResult = false
  PartialLoad = false
  Refine = true
  Relative = true
  Support = -> [Link[meter.,meter001.]]
  _Version = 2
FEATURE [Sketcher::SketchObject] Sketch004
  ArcFitTolerance = 1e-06
  AttachmentSupport = -> [DatumPlane002]
  ExternalGeometry = -> [Binder005,Binder006]
  FullyConstrained = true
  MakeInternals = false
  MapMode = 5
  Placement = pos=(88.5499,-6.858,7.62) rot=(0.707107,0,0.707107;3.14159rad)
  sketch-geometry (16):
    g0: LineSegment StartX=-17.272 StartY=15.942 StartZ=0 EndX=-17.272 EndY=-143.958 EndZ=0
    g1: LineSegment StartX=-17.272 StartY=-143.958 StartZ=0 EndX=17.256 EndY=-143.958 EndZ=0
    g2: LineSegment StartX=17.256 StartY=-143.958 StartZ=0 EndX=17.256 EndY=-72.704 EndZ=0
    g3: LineSegment StartX=17.256 StartY=-72.704 StartZ=0 EndX=79.01 EndY=-72.704 EndZ=0
    g4: LineSegment [constr] StartX=79.01 StartY=-72.704 StartZ=0 EndX=79.01 EndY=-55.312 EndZ=0
    g5: LineSegment StartX=79.01 StartY=-55.312 StartZ=0 EndX=17.256 EndY=-55.312 EndZ=0
    g6: LineSegment StartX=17.256 StartY=-55.312 StartZ=0 EndX=17.256 EndY=15.942 EndZ=0
    g7: LineSegment StartX=17.256 StartY=15.942 StartZ=0 EndX=-17.272 EndY=15.942 EndZ=0
    g8: LineSegment StartX=89.17 StartY=15.942 StartZ=0 EndX=89.17 EndY=-143.958 EndZ=0
    g9: LineSegment StartX=89.17 StartY=15.942 StartZ=0 EndX=79.264 EndY=15.942 EndZ=0
    g10: LineSegment StartX=79.264 StartY=15.942 StartZ=0 EndX=79.264 EndY=-55.312 EndZ=0
    g11: LineSegment StartX=79.264 StartY=-72.704 StartZ=0 EndX=79.264 EndY=-143.958 EndZ=0
    g12: LineSegment StartX=79.264 StartY=-143.958 StartZ=0 EndX=89.17 EndY=-143.958 EndZ=0
    g13: LineSegment [constr] StartX=79.01 StartY=-72.958 StartZ=0 EndX=79.264 EndY=-72.958 EndZ=0
    g14: LineSegment StartX=79.264 StartY=-55.312 StartZ=0 EndX=79.01 EndY=-55.312 EndZ=0
    g15: LineSegment StartX=79.264 StartY=-72.704 StartZ=0 EndX=79.01 EndY=-72.704 EndZ=0
  constraints (41):
    c: Coincident(g0,g-6)
    c: Coincident(g0,g-6)
    c: Coincident(g1,g0)
    c: Coincident(g2,g1)
    c: Coincident(g3,g2)
    c: Horizontal(g3)
    c: Coincident(g4,g3)
    c: Coincident(g5,g4)
    c: Horizontal(g5)
    c: Coincident(g6,g5)
    c: Vertical(g6)
    c: Coincident(g7,g6)
    c: Coincident(g7,g0)
    c: Horizontal(g7)
    c: PointOnObject(g-8,g1)
    c: Tangent(g2,g6)
    c: DistanceX(g6,g-7) = 0.254
    c: PointOnObject(g-9,g4)
    c: PointOnObject(g-10,g4)
    c: DistanceY(g4,g-9) = 0.254
    c: DistanceY(g-10,g3) = 0.254
    c: Coincident(g8,g-11)
    c: Coincident(g8,g-11)
    c: Coincident(g9,g8)
    c: Horizontal(g9)
    c: Coincident(g10,g9)
    c: Vertical(g10)
    c: Coincident(g12,g11)
    c: Coincident(g12,g8)
    c: Horizontal(g12)
    c: Tangent(g10,g11)
    c: Coincident(g13,g-10)
    c: PointOnObject(g13,g11)
    c: Horizontal(g13)
    c: DistanceX(g13,g13) = 0.254
    c: Coincident(g14,g10)
    c: Coincident(g14,g4)
    c: Horizontal(g14)
    c: Horizontal(g11,g3)
    c: Coincident(g15,g11)
    c: Coincident(g15,g3)
FEATURE [PartDesign::Pad] Pad002
  Direction = (1,0,-2e-16)
  Length = 1.651
  Length2 = 10
  Placement = pos=(88.5499,-6.858,7.62) rot=(0.707107,0,0.707107;3.14159rad)
  Profile = -> Sketch004
  ReferenceAxis = -> Sketch004 [N_Axis]
  Refine = true
  Suppressed = false
  Type = 0
FEATURE [Sketcher::SketchObject] Sketch005
  ArcFitTolerance = 1e-06
  AttachmentSupport = -> [DatumPlane002]
  ExternalGeometry = -> [Pad002]
  FullyConstrained = false
  MakeInternals = false
  MapMode = 5
  Placement = pos=(88.5499,-6.858,7.62) rot=(0.707107,0,0.707107;3.14159rad)
  sketch-geometry (24):
    g0: LineSegment StartX=-17.272 StartY=15.942 StartZ=0 EndX=17.256 EndY=15.942 EndZ=0
    g1: LineSegment StartX=17.256 StartY=15.942 StartZ=0 EndX=17.256 EndY=-55.312 EndZ=0
    g2: LineSegment StartX=17.256 StartY=-55.312 StartZ=0 EndX=79.264 EndY=-55.312 EndZ=0
    g3: LineSegment StartX=79.264 StartY=15.942 StartZ=0 EndX=89.17 EndY=15.942 EndZ=0
    g4: LineSegment StartX=89.17 StartY=15.942 StartZ=0 EndX=89.17 EndY=-143.958 EndZ=0
    g5: LineSegment StartX=89.17 StartY=-143.958 StartZ=0 EndX=79.264 EndY=-143.958 EndZ=0
    g6: LineSegment StartX=17.256 StartY=-72.704 StartZ=0 EndX=17.256 EndY=-143.958 EndZ=0
    g7: LineSegment StartX=17.256 StartY=-143.958 StartZ=0 EndX=-17.272 EndY=-143.958 EndZ=0
    g8: LineSegment StartX=-17.272 StartY=15.942 StartZ=0 EndX=-17.272 EndY=-143.958 EndZ=0
    g9: LineSegment StartX=-15.621 StartY=14.291 StartZ=0 EndX=-15.621 EndY=-142.307 EndZ=0
    g10: LineSegment StartX=-15.621 StartY=-142.307 StartZ=0 EndX=15.605 EndY=-142.307 EndZ=0
    g11: LineSegment StartX=15.605 StartY=-142.307 StartZ=0 EndX=15.605 EndY=-71.053 EndZ=0
    g12: LineSegment StartX=15.605 StartY=-71.053 StartZ=0 EndX=79.264 EndY=-71.053 EndZ=0
    g13: LineSegment StartX=-15.621 StartY=14.291 StartZ=0 EndX=15.605 EndY=14.291 EndZ=0
    g14: LineSegment StartX=15.605 StartY=14.291 StartZ=0 EndX=15.605 EndY=-56.963 EndZ=0
    g15: LineSegment StartX=15.605 StartY=-56.963 StartZ=0 EndX=79.264 EndY=-56.963 EndZ=0
    g16: LineSegment StartX=17.256 StartY=-72.704 StartZ=0 EndX=79.264 EndY=-72.704 EndZ=0
    g17: LineSegment [constr] StartX=79.264 StartY=-55.312 StartZ=0 EndX=79.264 EndY=-56.963 EndZ=0
    g18: LineSegment [constr] StartX=79.264 StartY=-71.053 StartZ=0 EndX=79.264 EndY=-72.704 EndZ=0
    g19: LineSegment [constr] StartX=-17.272 StartY=-64.008 StartZ=0 EndX=-15.621 EndY=-64.008 EndZ=0
    g20: LineSegment [constr] StartX=-0.008 StartY=15.942 StartZ=0 EndX=-0.008 EndY=14.291 EndZ=0
    g21: LineSegment StartX=79.264 StartY=-72.704 StartZ=0 EndX=79.264 EndY=-143.958 EndZ=0
    g22: LineSegment StartX=79.264 StartY=-71.053 StartZ=0 EndX=79.264 EndY=-56.963 EndZ=0
    g23: LineSegment StartX=79.264 StartY=15.942 StartZ=0 EndX=79.264 EndY=-55.312 EndZ=0
  constraints (57):
    c: Coincident(g0,g-9)
    c: Coincident(g0,g-9)
    c: Coincident(g1,g0)
    c: Coincident(g1,g-5)
    c: Coincident(g2,g1)
    c: Coincident(g2,g-5)
    c: Coincident(g3,g-4)
    c: Coincident(g4,g3)
    c: Coincident(g4,g-4)
    c: Coincident(g5,g4)
    c: Coincident(g6,g-10)
    c: Coincident(g7,g6)
    c: Coincident(g7,g-10)
    c: Coincident(g8,g0)
    c: Coincident(g8,g7)
    c: Vertical(g9)
    c: Coincident(g10,g9)
    c: Horizontal(g10)
    c: Coincident(g11,g10)
    c: Vertical(g11)
    c: Coincident(g12,g11)
    c: Coincident(g13,g9)
    c: Horizontal(g13)
    c: Coincident(g14,g13)
    c: Vertical(g14)
    c: Coincident(g15,g14)
    c: Horizontal(g15)
    c: Coincident(g16,g6)
    c: Coincident(g16,g-7)
    c: Coincident(g17,g2)
    c: Coincident(g17,g15)
    c: Coincident(g18,g12)
    c: Coincident(g18,g16)
    c: Coincident(g3,g-8)
    c: Vertical(g17)
    c: Vertical(g18)
    c: Equal(g17,g18)
    c: DistanceY(g15,g2) = 1.651
    c: Symmetric(g8,g8,g19)
    c: Symmetric(g9,g9,g19)
    c: Horizontal(g19)
    c: DistanceX(g19,g19) = 1.651
    c: Symmetric(g0,g0,g20)
    c: PointOnObject(g20,g13)
    c: Vertical(g20)
    c: DistanceY(g20,g20) = 1.651
    c: DistanceX(g13,g0) = 1.651
    c: Coincident(g-6,g6)
    c: DistanceX(g11,g6) = 1.651
    c: Horizontal(g12)
    c: Coincident(g21,g16)
    c: Coincident(g21,g5)
    c: Vertical(g21)
    c: Coincident(g22,g12)
    c: Coincident(g22,g15)
    c: Coincident(g23,g3)
    c: Coincident(g23,g2)
FEATURE [PartDesign::SubShapeBinder] Binder007
  BindCopyOnChange = 0
  BindMode = 0
  ClaimChildren = false
  Context = -> Part001 [Body001.Binder007.]
  Fuse = false
  MakeFace = true
  OffsetFill = false
  OffsetIntersection = false
  OffsetJoinType = 0
  OffsetOpenResult = false
  PartialLoad = false
  Refine = true
  Relative = true
  Support = -> [Link[PCB_Assembly.WP154A4SUREQBFZGC.,PCB_Assembly.WP154A4SUREQBFZGC001.,PCB_Assembly.WP154A4SUREQBFZGC002.,PCB_Assembly.WP154A4SUREQBFZGC003.,PCB_Assembly.WP154A4SUREQBFZGC004.,PCB_Assembly.WP154A4SUREQBFZGC005.]]
  _Version = 2
FEATURE [Sketcher::SketchObject] Sketch009
  ArcFitTolerance = 1e-06
  AttachmentSupport = -> [DatumPlane002]
  ExternalGeometry = -> [Binder005]
  FullyConstrained = true
  MakeInternals = false
  MapMode = 5
  Placement = pos=(88.5499,-6.858,7.62) rot=(0.707107,0,0.707107;3.14159rad)
  sketch-geometry (15):
    g0: LineSegment StartX=7.8613 StartY=-127.508 StartZ=0 EndX=-7.8613 EndY=-127.508 EndZ=0
    g1: LineSegment StartX=-7.8613 StartY=-127.508 StartZ=0 EndX=-7.8613 EndY=-140.208 EndZ=0
    g2: LineSegment StartX=-7.8613 StartY=-140.208 StartZ=0 EndX=7.8613 EndY=-140.208 EndZ=0
    g3: LineSegment StartX=7.8613 StartY=-140.208 StartZ=0 EndX=7.8613 EndY=-127.508 EndZ=0
    g4: LineSegment [constr] StartX=5.74571 StartY=-137.858 StartZ=0 EndX=5.74571 EndY=-129.858 EndZ=0
    g5: LineSegment [constr] StartX=5.74571 StartY=-133.858 StartZ=0 EndX=7.8613 EndY=-133.858 EndZ=0
    g6: LineSegment [constr] StartX=5.74571 StartY=-129.858 StartZ=0 EndX=-5.74571 EndY=-129.858 EndZ=0
    g7: LineSegment [constr] StartX=5.74571 StartY=-129.858 StartZ=0 EndX=-5.74571 EndY=-129.858 EndZ=0
    g8: LineSegment [constr] StartX=-9e-16 StartY=-129.858 StartZ=0 EndX=-2.2e-15 EndY=-127.508 EndZ=0
    g9: LineSegment [constr] StartX=-5.74571 StartY=-137.858 StartZ=0 EndX=-5.74571 EndY=-129.858 EndZ=0
    g10: LineSegment [constr] StartX=-5.74571 StartY=-133.858 StartZ=0 EndX=-7.8613 EndY=-133.858 EndZ=0
    g11: LineSegment [constr] StartX=5.74571 StartY=-137.858 StartZ=0 EndX=-5.74571 EndY=-137.858 EndZ=0
    g12: LineSegment [constr] StartX=-9e-16 StartY=-137.858 StartZ=0 EndX=-2.2e-15 EndY=-140.208 EndZ=0
    g13: Circle CenterX=0 CenterY=0 CenterZ=0 NormalX=0 NormalY=0 NormalZ=1 AngleXU=0 Radius=3.683
    g14: Circle CenterX=-7.7978 CenterY=0 CenterZ=0 NormalX=0 NormalY=0 NormalZ=1 AngleXU=0 Radius=1.4986
  constraints (35):
    c: Coincident(g0,g1)
    c: Coincident(g1,g2)
    c: Coincident(g2,g3)
    c: Coincident(g3,g0)
    c: Horizontal(g2)
    c: Vertical(g1)
    c: Vertical(g3)
    c: DistanceY(g3,g3) = 12.7
    c: DistanceX(g0,g0) = 15.7226
    c: Coincident(g4,g-5)
    c: Coincident(g4,g-4)
    c: Symmetric(g4,g4,g5)
    c: Symmetric(g3,g3,g5)
    c: Coincident(g6,g4)
    c: Coincident(g6,g-4)
    c: Coincident(g7,g4)
    c: Coincident(g7,g6)
    c: Symmetric(g6,g6,g8)
    c: Symmetric(g0,g0,g8)
    c: Parallel(g2,g0)
    c: Coincident(g9,g-5)
    c: Coincident(g9,g6)
    c: Symmetric(g9,g9,g10)
    c: Symmetric(g1,g1,g10)
    c: Equal(g5,g10)
    c: Coincident(g11,g4)
    c: Coincident(g11,g9)
    c: Symmetric(g11,g11,g12)
    c: Symmetric(g2,g2,g12)
    c: Equal(g12,g8)
    c: Coincident(g13,g-1)
    c: Diameter(g13) = 7.366
    c: Diameter(g14) = 2.9972
    c: Horizontal(g13,g14)
    c: DistanceX(g14,g13) = 7.7978
FEATURE [Sketcher::SketchObject] Sketch026
  ArcFitTolerance = 1e-06
  AttachmentSupport = -> [DatumPlane002]
  FullyConstrained = false
  MakeInternals = false
  MapMode = 5
  Placement = pos=(88.5499,-6.858,7.62) rot=(0.707107,0,0.707107;3.14159rad)
  sketch-geometry (23):
    g0: LineSegment [constr] StartX=-5.969 StartY=4.512 StartZ=0 EndX=-5.969 EndY=15.688 EndZ=0
    g1: LineSegment StartX=-5.969 StartY=15.688 StartZ=0 EndX=-17.145 EndY=15.688 EndZ=0
    g2: LineSegment StartX=-17.145 StartY=15.688 StartZ=0 EndX=-17.145 EndY=4.512 EndZ=0
    g3: LineSegment [constr] StartX=-17.145 StartY=4.512 StartZ=0 EndX=-5.969 EndY=4.512 EndZ=0
    g4: GeomPoint [constr] X=-11.557 Y=10.1 Z=0
    g5: LineSegment StartX=-5.969 StartY=15.688 StartZ=0 EndX=-5.969 EndY=6.93092 EndZ=0
    g6: LineSegment StartX=-5.969 StartY=6.93092 StartZ=0 EndX=-7.95666 EndY=4.512 EndZ=0
    g7: LineSegment StartX=-7.95666 StartY=4.512 StartZ=0 EndX=-17.145 EndY=4.512 EndZ=0
    g8: LineSegment [constr] StartX=0 StartY=0 StartZ=0 EndX=-6.96283 EndY=5.72146 EndZ=0
    g9: GeomPoint [constr] X=-6.76659 Y=5.5602 Z=0
    g10: LineSegment StartX=-5.969 StartY=-110.938 StartZ=0 EndX=-17.145 EndY=-110.938 EndZ=0
    g11: LineSegment StartX=-17.145 StartY=-110.938 StartZ=0 EndX=-17.145 EndY=-122.114 EndZ=0
    g12: LineSegment StartX=-17.145 StartY=-122.114 StartZ=0 EndX=-5.969 EndY=-122.114 EndZ=0
    g13: LineSegment StartX=-5.969 StartY=-122.114 StartZ=0 EndX=-5.969 EndY=-110.938 EndZ=0
    g14: GeomPoint [constr] X=-11.557 Y=-116.526 Z=0
    g15: Circle CenterX=-11.557 CenterY=10.1 CenterZ=0 NormalX=0 NormalY=0 NormalZ=1 AngleXU=0 Radius=1.524
    g16: Circle CenterX=-11.557 CenterY=-116.526 CenterZ=0 NormalX=0 NormalY=0 NormalZ=1 AngleXU=0 Radius=1.524
    g17: LineSegment StartX=53.848 StartY=-69.596 StartZ=0 EndX=53.848 EndY=-58.42 EndZ=0
    g18: LineSegment StartX=53.848 StartY=-58.42 StartZ=0 EndX=42.672 EndY=-58.42 EndZ=0
    g19: LineSegment StartX=42.672 StartY=-58.42 StartZ=0 EndX=42.672 EndY=-69.596 EndZ=0
    g20: LineSegment StartX=42.672 StartY=-69.596 StartZ=0 EndX=53.848 EndY=-69.596 EndZ=0
    g21: GeomPoint [constr] X=48.26 Y=-64.008 Z=0
    g22: Circle CenterX=48.26 CenterY=-64.008 CenterZ=0 NormalX=0 NormalY=0 NormalZ=1 AngleXU=0 Radius=1.524
  constraints (52):
    c: Coincident(g0,g1)
    c: Coincident(g1,g2)
    c: Coincident(g2,g3)
    c: Coincident(g3,g0)
    c: Vertical(g0)
    c: Vertical(g2)
    c: Horizontal(g1)
    c: Horizontal(g3)
    c: Symmetric(g2,g0,g4)
    c: Coincident(g4,g-3)
    c: Equal(g1,g0)
    c: DistanceX(g1,g1) = 11.176
    c: Coincident(g5,g0)
    c: PointOnObject(g5,g0)
    c: Coincident(g6,g5)
    c: PointOnObject(g6,g3)
    c: Coincident(g7,g6)
    c: Coincident(g7,g2)
    c: Coincident(g8,g-1)
    c: Symmetric(g6,g6,g8)
    c: Perpendicular(g6,g8)
    c: PointOnObject(g9,g8)
    c: PointOnObject(g9,g-5)
    c: Distance(g9,g8) = 0.254
    c: Coincident(g10,g11)
    c: Coincident(g11,g12)
    c: Coincident(g12,g13)
    c: Coincident(g13,g10)
    c: Horizontal(g10)
    c: Horizontal(g12)
    c: Vertical(g11)
    c: Vertical(g13)
    c: Symmetric(g12,g10,g14)
    c: Coincident(g14,g-4)
    c: Equal(g13,g10)
    c: Equal(g10,g2)
    c: Coincident(g15,g4)
    c: Coincident(g16,g14)
    c: Coincident(g17,g18)
    c: Coincident(g18,g19)
    c: Coincident(g19,g20)
    c: Coincident(g20,g17)
    c: Vertical(g17)
    c: Vertical(g19)
    c: Horizontal(g18)
    c: Horizontal(g20)
    c: Symmetric(g19,g17,g21)
    c: Coincident(g21,g-6)
    c: Equal(g18,g19)
    c: Equal(g19,g1)
    c: Coincident(g22,g21)
    c: Equal(g-6,g22)
FEATURE [PartDesign::Plane] DatumPlane024  label="bottom nut slot"
  Length = 191.716
  MapMode = 5
  Placement = pos=(88.5499,-6.858,1.651) rot=(0,0,-1;1.5708rad)
  ResizeMode = 0
  Width = 142.73
FEATURE [Sketcher::SketchObject] Sketch067
  ArcFitTolerance = 1e-06
  AttachmentSupport = -> [DatumPlane024]
  FullyConstrained = true
  MakeInternals = false
  MapMode = 5
  Placement = pos=(88.5499,-6.858,1.651) rot=(0,0,-1;1.5708rad)
  sketch-geometry (15):
    g0: LineSegment StartX=-119.701 StartY=-4.66644 StartZ=0 EndX=-119.701 EndY=-7.33344 EndZ=0
    g1: LineSegment StartX=-119.701 StartY=-7.33344 StartZ=0 EndX=-113.351 EndY=-7.33344 EndZ=0
    g2: LineSegment StartX=-113.351 StartY=-7.33344 StartZ=0 EndX=-113.351 EndY=-4.66644 EndZ=0
    g3: LineSegment StartX=-113.351 StartY=-4.66644 StartZ=0 EndX=-119.701 EndY=-4.66644 EndZ=0
    g4: LineSegment StartX=6.925 StartY=-4.66644 StartZ=0 EndX=6.925 EndY=-7.33344 EndZ=0
    g5: LineSegment StartX=6.925 StartY=-7.33344 StartZ=0 EndX=13.275 EndY=-7.33344 EndZ=0
    g6: LineSegment StartX=13.275 StartY=-7.33344 StartZ=0 EndX=13.275 EndY=-4.66644 EndZ=0
    g7: LineSegment StartX=13.275 StartY=-4.66644 StartZ=0 EndX=6.925 EndY=-4.66644 EndZ=0
    g8: GeomPoint X=10.1 Y=-11.9999 Z=0
    g9: GeomPoint X=10.1 Y=-7.33344 Z=0
    g10: GeomPoint X=-116.526 Y=-11.9999 Z=0
    g11: GeomPoint X=-116.526 Y=-7.33344 Z=0
    g12: LineSegment [constr] StartX=-122.114 StartY=1.563e-13 StartZ=0 EndX=-118.05 EndY=-11.9999 EndZ=0
    g13: GeomPoint [constr] X=-120.082 Y=-5.99994 Z=0
    g14: GeomPoint [constr] X=-119.701 Y=-5.99994 Z=0
  constraints (31):
    c: Coincident(g0,g1)
    c: Coincident(g1,g2)
    c: Coincident(g2,g3)
    c: Coincident(g3,g0)
    c: Vertical(g0)
    c: Vertical(g2)
    c: Horizontal(g1)
    c: Horizontal(g3)
    c: Coincident(g4,g5)
    c: Coincident(g5,g6)
    c: Coincident(g6,g7)
    c: Coincident(g7,g4)
    c: Vertical(g4)
    c: Vertical(g6)
    c: PointOnObject(g2,g7)
    c: Tangent(g3,g7,g2) = -1.5708
    c: Tangent(g5,g1)
    c: Equal(g1,g5)
    c: Symmetric(g5,g5,g9)
    c: Symmetric(g-4,g-4,g8)
    c: Vertical(g9,g8)
    c: Symmetric(g0,g1,g11)
    c: Symmetric(g-3,g-3,g10)
    c: Vertical(g11,g10)
    c: Coincident(g12,g-5)
    c: Coincident(g12,g-3)
    c: Symmetric(g0,g0,g14)
    c: Symmetric(g12,g12,g13)
    c: Horizontal(g14,g13)
    c: DistanceX(g0,g1) = 6.35
    c: DistanceY(g1,g2) = 2.667
FEATURE [PartDesign::Plane] DatumPlane040  label="sub panel front"
  AttachmentSupport = -> [Binder004]
  Length = 192.491
  MapMode = 5
  Placement = pos=(76.55,0,0) rot=(0.57735,0.57735,0.57735;2.0944rad)
  ResizeMode = 0
  Width = 150.095
FEATURE [PartDesign::Pad] Pad003
  BaseFeature = -> Pad002
  Direction = (1,0,-2e-16)
  Length = 9.99998
  Length2 = 9.99998
  Placement = pos=(88.5499,-6.858,7.62) rot=(0.707107,0,0.707107;3.14159rad)
  Profile = -> Sketch005
  ReferenceAxis = -> Sketch005 [N_Axis]
  Refine = true
  Suppressed = false
  Type = 3
  UpToFace = -> DatumPlane040
FEATURE [PartDesign::Pad] Pad005  label="nut posts"
  BaseFeature = -> Pad003
  Direction = (1,0,-2e-16)
  Length = 6.35
  Length2 = 10
  Placement = pos=(88.5499,-6.858,7.62) rot=(0.707107,0,0.707107;3.14159rad)
  Profile = -> Sketch026
  ReferenceAxis = -> Sketch026 [N_Axis]
  Refine = true
  Reversed = true
  Suppressed = false
  Type = 3
  UpToFace = -> Pad003 [Face1]
FEATURE [PartDesign::Fillet] Fillet
  Base = -> Pad005 [Edge33]
  BaseFeature = -> Pad005
  Placement = pos=(88.5499,-6.858,7.62) rot=(0.707107,0,0.707107;3.14159rad)
  Radius = 2.54
  Refine = true
  SupportTransform = false
  Suppressed = false
  UseAllEdges = false
FEATURE [Sketcher::SketchObject] Sketch023
  ArcFitTolerance = 1e-06
  AttachmentSupport = -> [DatumPlane002]
  ExternalGeometry = -> [Fillet]
  FullyConstrained = true
  MakeInternals = false
  MapMode = 5
  Placement = pos=(88.5499,-6.858,7.62) rot=(0.707107,0,0.707107;3.14159rad)
  sketch-geometry (14):
    g0: LineSegment StartX=85.995 StartY=3.242 StartZ=0 EndX=79.264 EndY=3.242 EndZ=0
    g1: LineSegment StartX=79.264 StartY=3.242 StartZ=0 EndX=79.264 EndY=-52.772 EndZ=0
    g2: LineSegment StartX=79.264 StartY=-52.772 StartZ=0 EndX=85.995 EndY=-52.772 EndZ=0
    g3: LineSegment StartX=85.995 StartY=-52.772 StartZ=0 EndX=85.995 EndY=3.242 EndZ=0
    g4: LineSegment StartX=79.264 StartY=-75.244 StartZ=0 EndX=79.264 EndY=-131.258 EndZ=0
    g5: LineSegment StartX=79.264 StartY=-131.258 StartZ=0 EndX=85.995 EndY=-131.258 EndZ=0
    g6: LineSegment StartX=85.995 StartY=-131.258 StartZ=0 EndX=85.995 EndY=-75.244 EndZ=0
    g7: LineSegment StartX=85.995 StartY=-75.244 StartZ=0 EndX=79.264 EndY=-75.244 EndZ=0
    g8: LineSegment [constr] StartX=85.995 StartY=-131.258 StartZ=0 EndX=85.995 EndY=-143.958 EndZ=0
    g9: LineSegment [constr] StartX=85.995 StartY=-143.958 StartZ=0 EndX=79.264 EndY=-143.958 EndZ=0
    g10: LineSegment [constr] StartX=85.995 StartY=3.242 StartZ=0 EndX=89.17 EndY=3.242 EndZ=0
    g11: LineSegment [constr] StartX=89.17 StartY=3.242 StartZ=0 EndX=89.17 EndY=15.942 EndZ=0
    g12: LineSegment [constr] StartX=79.264 StartY=-52.772 StartZ=0 EndX=79.264 EndY=-55.312 EndZ=0
    g13: LineSegment [constr] StartX=79.264 StartY=-72.704 StartZ=0 EndX=79.264 EndY=-75.244 EndZ=0
  constraints (36):
    c: Coincident(g0,g1)
    c: Coincident(g1,g2)
    c: Coincident(g2,g3)
    c: Coincident(g3,g0)
    c: Horizontal(g0)
    c: Horizontal(g2)
    c: Vertical(g1)
    c: Vertical(g3)
    c: DistanceY(g0,g-4) = 12.7
    c: Vertical(g0,g-4)
    c: DistanceY(g-5,g1) = 2.54
    c: Coincident(g4,g5)
    c: Coincident(g5,g6)
    c: Coincident(g6,g7)
    c: Coincident(g7,g4)
    c: Horizontal(g5)
    c: Horizontal(g7)
    c: Coincident(g8,g5)
    c: Vertical(g8)
    c: Coincident(g9,g8)
    c: Coincident(g9,g-3)
    c: Horizontal(g9)
    c: Coincident(g10,g0)
    c: Coincident(g11,g10)
    c: Coincident(g11,g-4)
    c: Horizontal(g10)
    c: Tangent(g6,g3)
    c: Equal(g11,g8)
    c: Vertical(g11)
    c: Tangent(g1,g4)
    c: Coincident(g12,g1)
    c: Coincident(g12,g-5)
    c: Coincident(g13,g-7)
    c: Coincident(g13,g4)
    c: Equal(g13,g12)
    c: DistanceX(g0,g10) = 3.175
FEATURE [PartDesign::Pocket] Pocket007  label="hollow backlight area"
  BaseFeature = -> Fillet
  Direction = (-1,0,2e-16)
  Length = 12.7
  Length2 = 5
  Placement = pos=(88.5499,-6.858,7.62) rot=(0.707107,0,0.707107;3.14159rad)
  Profile = -> Sketch023
  ReferenceAxis = -> Sketch023 [N_Axis]
  Refine = true
  Suppressed = false
  Type = 1
FEATURE [Sketcher::SketchObject] Sketch024
  ArcFitTolerance = 1e-06
  AttachmentSupport = -> [DatumPlane002]
  ExternalGeometry = -> [Pocket007]
  FullyConstrained = true
  MakeInternals = false
  MapMode = 5
  Placement = pos=(88.5499,-6.858,7.62) rot=(0.707107,0,0.707107;3.14159rad)
  sketch-geometry (9):
    g0: LineSegment StartX=85.995 StartY=-52.772 StartZ=0 EndX=82.947 EndY=-52.772 EndZ=0
    g1: LineSegment [constr] StartX=82.947 StartY=-52.772 StartZ=0 EndX=82.947 EndY=-75.244 EndZ=0
    g2: LineSegment StartX=82.947 StartY=-75.244 StartZ=0 EndX=85.995 EndY=-75.244 EndZ=0
    g3: LineSegment StartX=85.995 StartY=-75.244 StartZ=0 EndX=85.995 EndY=-52.772 EndZ=0
    g4: LineSegment StartX=82.947 StartY=-52.772 StartZ=0 EndX=82.947 EndY=-59.122 EndZ=0
    g5: LineSegment StartX=82.947 StartY=-59.122 StartZ=0 EndX=79.264 EndY=-59.122 EndZ=0
    g6: LineSegment StartX=79.264 StartY=-59.122 StartZ=0 EndX=79.264 EndY=-68.894 EndZ=0
    g7: LineSegment StartX=79.264 StartY=-68.894 StartZ=0 EndX=82.947 EndY=-68.894 EndZ=0
    g8: LineSegment StartX=82.947 StartY=-68.894 StartZ=0 EndX=82.947 EndY=-75.244 EndZ=0
  constraints (24):
    c: Coincident(g0,g1)
    c: Coincident(g1,g2)
    c: Coincident(g2,g3)
    c: Coincident(g3,g0)
    c: Horizontal(g0)
    c: Horizontal(g2)
    c: Coincident(g0,g-3)
    c: Coincident(g2,g-4)
    c: DistanceX(g1,g2) = 3.048
    c: Coincident(g4,g0)
    c: PointOnObject(g4,g1)
    c: Vertical(g4)
    c: Coincident(g5,g4)
    c: Horizontal(g5)
    c: Coincident(g6,g5)
    c: Vertical(g6)
    c: Coincident(g7,g6)
    c: PointOnObject(g7,g1)
    c: Coincident(g8,g7)
    c: Coincident(g8,g1)
    c: Equal(g4,g8)
    c: PointOnObject(g-3,g6)
    c: Horizontal(g7)
    c: DistanceY(g4,g0) = 6.35
FEATURE [PartDesign::Pocket] Pocket008  label="more hollow"
  BaseFeature = -> Pocket007
  Direction = (-1,0,2e-16)
  Length = 5
  Length2 = 5
  Placement = pos=(88.5499,-6.858,7.62) rot=(0.707107,0,0.707107;3.14159rad)
  Profile = -> Sketch024
  ReferenceAxis = -> Sketch024 [N_Axis]
  Refine = true
  Suppressed = false
  Type = 1
FEATURE [Sketcher::SketchObject] Sketch066
  ArcFitTolerance = 1e-06
  AttachmentSupport = -> [Pocket008]
  ExternalGeometry = -> [Pocket008]
  FullyConstrained = true
  MakeInternals = false
  MapMode = 5
  Placement = pos=(88.5499,-6.858,61.468) rot=(0,0,-1;1.5708rad)
  sketch-geometry (8):
    g0: LineSegment StartX=-67.183 StartY=-4.66644 StartZ=0 EndX=-67.183 EndY=-7.33344 EndZ=0
    g1: LineSegment StartX=-67.183 StartY=-7.33344 StartZ=0 EndX=-60.833 EndY=-7.33344 EndZ=0
    g2: LineSegment StartX=-60.833 StartY=-7.33344 StartZ=0 EndX=-60.833 EndY=-4.66644 EndZ=0
    g3: LineSegment StartX=-60.833 StartY=-4.66644 StartZ=0 EndX=-67.183 EndY=-4.66644 EndZ=0
    g4: GeomPoint X=-64.008 Y=-11.9999 Z=0
    g5: GeomPoint X=-64.008 Y=-7.33344 Z=0
    g6: GeomPoint [constr] X=-60.833 Y=-5.99994 Z=0
    g7: GeomPoint [constr] X=-58.42 Y=-5.99994 Z=0
  constraints (16):
    c: Coincident(g0,g1)
    c: Coincident(g1,g2)
    c: Coincident(g2,g3)
    c: Coincident(g3,g0)
    c: Vertical(g0)
    c: Vertical(g2)
    c: Horizontal(g1)
    c: Horizontal(g3)
    c: DistanceX(g0,g2) = 6.35
    c: DistanceY(g1,g2) = 2.667
    c: Symmetric(g1,g0,g5)
    c: Symmetric(g-7,g-7,g4)
    c: Symmetric(g1,g2,g6)
    c: Symmetric(g-5,g-5,g7)
    c: Horizontal(g6,g7)
    c: Vertical(g4,g5)
FEATURE [PartDesign::Pocket] Pocket025  label="center nut slot"
  BaseFeature = -> Pocket008
  Direction = (0,0,-1)
  Length = 10.16
  Length2 = 5
  Placement = pos=(88.5499,-6.858,7.62) rot=(0.707107,0,0.707107;3.14159rad)
  Profile = -> Sketch066
  ReferenceAxis = -> Sketch066 [N_Axis]
  Refine = true
  Suppressed = false
  Type = 0
FEATURE [PartDesign::Pocket] Pocket004  label="front panel controls"
  BaseFeature = -> Pocket025
  Direction = (-1,0,2e-16)
  Length = 5
  Length2 = 5
  Placement = pos=(88.5499,-6.858,7.62) rot=(0.707107,0,0.707107;3.14159rad)
  Profile = -> Sketch009
  ReferenceAxis = -> Sketch009 [N_Axis]
  Refine = true
  Reversed = true
  Suppressed = false
  Type = 1
FEATURE [PartDesign::Plane] DatumPlane003  label="text plane"
  AttachmentOffset = pos=(0,0,-1) rot=(0,0,1;0rad)
  AttachmentSupport = -> [Pocket004]
  Length = 150.095
  MapMode = 5
  Placement = pos=(89.2009,-6.858,7.62) rot=(0.707107,0,0.707107;3.14159rad)
  ResizeMode = 0
  Width = 192.491
FEATURE [Sketcher::SketchObject] Sketch022
  ArcFitTolerance = 1e-06
  AttachmentSupport = -> [DatumPlane003]
  FullyConstrained = true
  MakeInternals = false
  MapMode = 5
  Placement = pos=(89.2009,-6.858,7.62) rot=(0.707107,0,0.707107;3.14159rad)
  sketch-geometry (47):
    g0: LineSegment StartX=-12.319 StartY=-7.814 StartZ=0 EndX=-13.716 EndY=-7.814 EndZ=0
    g1: LineSegment StartX=-13.716 StartY=-7.814 StartZ=0 EndX=-13.716 EndY=-11.37 EndZ=0
    g2: LineSegment StartX=-13.716 StartY=-11.37 StartZ=0 EndX=-12.319 EndY=-11.37 EndZ=0
    g3: LineSegment StartX=-12.319 StartY=-11.37 StartZ=0 EndX=-12.319 EndY=-7.814 EndZ=0
    g4: ArcOfCircle CenterX=0 CenterY=0 CenterZ=0 NormalX=0 NormalY=0 NormalZ=1 AngleXU=0 Radius=11.938 StartAngle=1.0472 EndAngle=2.26893
    g5: ArcOfCircle CenterX=0 CenterY=0 CenterZ=0 NormalX=0 NormalY=0 NormalZ=1 AngleXU=0 Radius=13.716 StartAngle=1.0472 EndAngle=2.26893
    g6: LineSegment StartX=-7.6736 StartY=9.14504 StartZ=0 EndX=-8.81647 EndY=10.5071 EndZ=0
    g7: LineSegment [constr] StartX=6.858 StartY=11.8784 StartZ=0 EndX=5.969 EndY=10.3386 EndZ=0
    g8: LineSegment StartX=5.207 StartY=9.01879 StartZ=0 EndX=5.969 EndY=10.3386 EndZ=0
    g9: LineSegment StartX=6.858 StartY=11.8784 StartZ=0 EndX=7.62 EndY=13.1982 EndZ=0
    g10: LineSegment StartX=5.207 StartY=9.01879 StartZ=0 EndX=8.2374 EndY=10.0555 EndZ=0
    g11: LineSegment StartX=8.2374 StartY=10.0555 StartZ=0 EndX=7.62 EndY=13.1982 EndZ=0
    g12: ArcOfCircle CenterX=0 CenterY=0 CenterZ=0 NormalX=0 NormalY=0 NormalZ=1 AngleXU=0 Radius=11.938 StartAngle=4.01426 EndAngle=5.23599
    g13: ArcOfCircle CenterX=0 CenterY=0 CenterZ=0 NormalX=0 NormalY=0 NormalZ=1 AngleXU=0 Radius=13.716 StartAngle=4.01426 EndAngle=5.23599
    g14: LineSegment StartX=-7.6736 StartY=-9.14504 StartZ=0 EndX=-8.81647 EndY=-10.5071 EndZ=0
    g15: LineSegment [constr] StartX=5.969 StartY=-10.3386 StartZ=0 EndX=6.858 EndY=-11.8784 EndZ=0
    g16: LineSegment StartX=5.969 StartY=-10.3386 StartZ=0 EndX=5.207 EndY=-9.01879 EndZ=0
    g17: LineSegment StartX=5.207 StartY=-9.01879 StartZ=0 EndX=8.2374 EndY=-10.0555 EndZ=0
    g18: LineSegment StartX=8.2374 StartY=-10.0555 StartZ=0 EndX=7.62 EndY=-13.1982 EndZ=0
    g19: LineSegment StartX=7.62 StartY=-13.1982 StartZ=0 EndX=6.858 EndY=-11.8784 EndZ=0
    g20: LineSegment [constr] StartX=0 StartY=0 StartZ=0 EndX=-12.7 EndY=0 EndZ=0
    g21: LineSegment [constr] StartX=-12.319 StartY=12.005 StartZ=0 EndX=-13.716 EndY=12.005 EndZ=0
    g22: LineSegment [constr] StartX=-13.716 StartY=12.005 StartZ=0 EndX=-13.716 EndY=7.814 EndZ=0
    g23: LineSegment [constr] StartX=-13.716 StartY=7.814 StartZ=0 EndX=-12.319 EndY=7.814 EndZ=0
    g24: LineSegment [constr] StartX=-12.319 StartY=7.814 StartZ=0 EndX=-12.319 EndY=12.005 EndZ=0
    g25: LineSegment [constr] StartX=-10.922 StartY=10.608 StartZ=0 EndX=-15.113 EndY=10.608 EndZ=0
    g26: LineSegment [constr] StartX=-15.113 StartY=10.608 StartZ=0 EndX=-15.113 EndY=9.211 EndZ=0
    g27: LineSegment [constr] StartX=-15.113 StartY=9.211 StartZ=0 EndX=-10.922 EndY=9.211 EndZ=0
    g28: LineSegment [constr] StartX=-10.922 StartY=9.211 StartZ=0 EndX=-10.922 EndY=10.608 EndZ=0
    g29: LineSegment [constr] StartX=-10.922 StartY=9.211 StartZ=0 EndX=-15.113 EndY=10.608 EndZ=0
    g30: LineSegment [constr] StartX=-13.716 StartY=7.814 StartZ=0 EndX=-12.319 EndY=12.005 EndZ=0
    g31: GeomPoint [constr] X=-13.0175 Y=9.9095 Z=0
    g32: GeomPoint [constr] X=-13.0175 Y=9.9095 Z=0
    g33: LineSegment [constr] StartX=-12.319 StartY=7.814 StartZ=0 EndX=-12.319 EndY=-7.814 EndZ=0
    g34: LineSegment [constr] StartX=0 StartY=0 StartZ=0 EndX=-12.319 EndY=0 EndZ=0
    g35: LineSegment StartX=-15.113 StartY=10.608 StartZ=0 EndX=-15.113 EndY=9.211 EndZ=0
    g36: LineSegment StartX=-15.113 StartY=9.211 StartZ=0 EndX=-13.716 EndY=9.211 EndZ=0
    g37: LineSegment StartX=-13.716 StartY=9.211 StartZ=0 EndX=-13.716 EndY=7.814 EndZ=0
    g38: LineSegment StartX=-13.716 StartY=7.814 StartZ=0 EndX=-12.319 EndY=7.814 EndZ=0
    g39: LineSegment StartX=-12.319 StartY=7.814 StartZ=0 EndX=-12.319 EndY=9.211 EndZ=0
    g40: LineSegment StartX=-12.319 StartY=9.211 StartZ=0 EndX=-10.922 EndY=9.211 EndZ=0
    g41: LineSegment StartX=-10.922 StartY=9.211 StartZ=0 EndX=-10.922 EndY=10.608 EndZ=0
    g42: LineSegment StartX=-10.922 StartY=10.608 StartZ=0 EndX=-12.319 EndY=10.608 EndZ=0
    g43: LineSegment StartX=-12.319 StartY=10.608 StartZ=0 EndX=-12.319 EndY=12.005 EndZ=0
    g44: LineSegment StartX=-12.319 StartY=12.005 StartZ=0 EndX=-13.716 EndY=12.005 EndZ=0
    g45: LineSegment StartX=-13.716 StartY=12.005 StartZ=0 EndX=-13.716 EndY=10.608 EndZ=0
    g46: LineSegment StartX=-15.113 StartY=10.608 StartZ=0 EndX=-13.716 EndY=10.608 EndZ=0
  constraints (123):
    c: Coincident(g0,g1)
    c: Coincident(g1,g2)
    c: Coincident(g2,g3)
    c: Coincident(g3,g0)
    c: Horizontal(g0)
    c: Horizontal(g2)
    c: Vertical(g1)
    c: Vertical(g3)
    c: DistanceY(g3,g3) = 3.556
    c: Radius(g4) = 11.938
    c: Coincident(g6,g4)
    c: Coincident(g5,g7)
    c: Coincident(g5,g6)
    c: Equal(g8,g9)
    c: Coincident(g4,g8)
    c: Coincident(g9,g5)
    c: Coincident(g7,g4)
    c: Coincident(g4,g-1)
    c: Coincident(g4,g5)
    c: PointOnObject(g4,g6)
    c: PointOnObject(g4,g7)
    c: PointOnObject(g4,g8)
    c: PointOnObject(g4,g9)
    c: Coincident(g11,g9)
    c: Coincident(g11,g10)
    c: Coincident(g10,g8)
    c: Equal(g11,g10)
    c: Distance(g6,g6) = 1.778
    c: Distance(g5,g10) = 2.286
    c: Angle(g8,g6) = 1.22173
    c: Equal(g12,g4)
    c: Coincident(g12,g4)
    c: Equal(g5,g13)
    c: Coincident(g13,g14)
    c: Coincident(g12,g14)
    c: Perpendicular(g12,g14)
    c: PointOnObject(g4,g15)
    c: Coincident(g12,g15)
    c: Coincident(g15,g13)
    c: Coincident(g13,g4)
    c: Vertical(g4,g12)
    c: Vertical(g4,g12)
    c: Coincident(g12,g16)
    c: Coincident(g16,g17)
    c: Coincident(g18,g19)
    c: Coincident(g19,g13)
    c: Coincident(g18,g17)
    c: Equal(g17,g18)
    c: Equal(g17,g10)
    c: PointOnObject(g4,g16)
    c: PointOnObject(g4,g19)
    c: Equal(g16,g19)
    c: Equal(g16,g8)
    c: Distance(g5,g9) = 1.524
    c: Angle(g6,g20) = 0.872665
    c: Coincident(g20,g4)
    c: DistanceX(g20,g4) = 12.7
    c: Coincident(g21,g22)
    c: Coincident(g22,g23)
    c: Coincident(g23,g24)
    c: Coincident(g24,g21)
    c: Horizontal(g21)
    c: Horizontal(g23)
    c: Vertical(g22)
    c: Vertical(g24)
    c: Coincident(g25,g26)
    c: Coincident(g26,g27)
    c: Coincident(g27,g28)
    c: Coincident(g28,g25)
    c: Horizontal(g25)
    c: Horizontal(g27)
    c: Vertical(g26)
    c: Vertical(g28)
    c: DistanceY(g28,g28) = 1.397
    c: Equal(g28,g23)
    c: Equal(g24,g27)
    c: DistanceX(g26,g27) = 4.191
    c: Symmetric(g30,g30,g32)
    c: Symmetric(g29,g29,g31)
    c: Coincident(g31,g32)
    c: Coincident(g30,g22)
    c: Coincident(g21,g30)
    c: Coincident(g29,g27)
    c: Coincident(g29,g25)
    c: Vertical(g33)
    c: Coincident(g0,g33)
    c: Symmetric(g33,g0,g34)
    c: Coincident(g23,g33)
    c: Horizontal(g34)
    c: Coincident(g4,g34)
    c: DistanceX(g2,g2) = 1.397
    c: DistanceX(g-4,g26) = 0.508
    c: DistanceY(g26,g-4) = 5.08
    c: Horizontal(g20)
    c: Coincident(g35,g25)
    c: Coincident(g35,g26)
    c: Coincident(g36,g26)
    c: PointOnObject(g36,g22)
    c: Horizontal(g36)
    c: PointOnObject(g37,g22)
    c: Coincident(g37,g22)
    c: Coincident(g38,g22)
    c: Coincident(g38,g23)
    c: Coincident(g39,g23)
    c: PointOnObject(g39,g24)
    c: Coincident(g40,g39)
    c: Coincident(g40,g27)
    c: Horizontal(g40)
    c: Coincident(g41,g27)
    c: Coincident(g41,g25)
    c: Coincident(g42,g25)
    c: PointOnObject(g42,g25)
    c: Coincident(g43,g42)
    c: Coincident(g43,g21)
    c: Vertical(g43)
    c: Coincident(g44,g21)
    c: Coincident(g44,g21)
    c: Coincident(g45,g21)
    c: PointOnObject(g45,g22)
    c: PointOnObject(g37,g36)
    c: Coincident(g46,g25)
    c: Coincident(g46,g45)
    c: Horizontal(g46)
FEATURE [Sketcher::SketchObject] Sketch064
  ArcFitTolerance = 1e-06
  AttachmentSupport = -> [Pocket004]
  ExternalGeometry = -> [Pocket004]
  FullyConstrained = true
  MakeInternals = false
  MapMode = 5
  Placement = pos=(88.5499,-6.858,86.884) rot=(0.707107,0.707107,0;3.14159rad)
  sketch-geometry (15):
    g0: LineSegment StartX=-13.402 StartY=-5.11094 StartZ=0 EndX=-13.402 EndY=-7.77794 EndZ=0
    g1: LineSegment StartX=-13.402 StartY=-7.77794 StartZ=0 EndX=-7.052 EndY=-7.77794 EndZ=0
    g2: LineSegment StartX=-7.052 StartY=-7.77794 StartZ=0 EndX=-7.052 EndY=-5.11094 EndZ=0
    g3: LineSegment StartX=-7.052 StartY=-5.11094 StartZ=0 EndX=-13.402 EndY=-5.11094 EndZ=0
    g4: GeomPoint [constr] X=-10.227 Y=-7.77794 Z=0
    g5: LineSegment [constr] StartX=-10.227 StartY=-11.9999 StartZ=0 EndX=-10.227 EndY=-7.77794 EndZ=0
    g6: LineSegment [constr] StartX=-11.751 StartY=-11.9999 StartZ=0 EndX=-15.942 EndY=-0.889 EndZ=0
    g7: GeomPoint [constr] X=-13.402 Y=-6.44444 Z=0
    g8: GeomPoint [constr] X=-13.8465 Y=-6.44444 Z=0
    g9: LineSegment StartX=135.068 StartY=-5.11094 StartZ=0 EndX=135.068 EndY=-7.77794 EndZ=0
    g10: LineSegment StartX=135.068 StartY=-7.77794 StartZ=0 EndX=141.418 EndY=-7.77794 EndZ=0
    g11: LineSegment StartX=141.418 StartY=-7.77794 StartZ=0 EndX=141.418 EndY=-5.11094 EndZ=0
    g12: LineSegment StartX=141.418 StartY=-5.11094 StartZ=0 EndX=135.068 EndY=-5.11094 EndZ=0
    g13: GeomPoint X=138.243 Y=-11.9999 Z=0
    g14: GeomPoint X=138.243 Y=-7.77794 Z=0
  constraints (31):
    c: Coincident(g0,g1)
    c: Coincident(g1,g2)
    c: Coincident(g2,g3)
    c: Coincident(g3,g0)
    c: Vertical(g0)
    c: Vertical(g2)
    c: Horizontal(g1)
    c: Horizontal(g3)
    c: DistanceX(g0,g2) = 6.35
    c: DistanceY(g1,g2) = 2.667
    c: Symmetric(g1,g0,g4)
    c: Symmetric(g-4,g-4,g5)
    c: Coincident(g5,g4)
    c: Vertical(g5)
    c: Coincident(g6,g-4)
    c: Coincident(g6,g-5)
    c: Symmetric(g0,g0,g7)
    c: Symmetric(g6,g6,g8)
    c: Horizontal(g7,g8)
    c: Coincident(g9,g10)
    c: Coincident(g10,g11)
    c: Coincident(g11,g12)
    c: Coincident(g12,g9)
    c: Vertical(g9)
    c: Vertical(g11)
    c: Tangent(g12,g3)
    c: Tangent(g10,g1)
    c: Equal(g1,g10)
    c: Symmetric(g10,g10,g14)
    c: Symmetric(g-6,g-6,g13)
    c: Vertical(g13,g14)
FEATURE [PartDesign::Pocket] Pocket023  label="nut slots001"
  BaseFeature = -> Pocket004
  Direction = (0,0,1)
  Length = 8.382
  Length2 = 5
  Placement = pos=(88.5499,-6.858,7.62) rot=(0.707107,0,0.707107;3.14159rad)
  Profile = -> Sketch064
  ReferenceAxis = -> Sketch064 [N_Axis]
  Refine = true
  Suppressed = false
  Type = 0
FEATURE [Sketcher::SketchObject] Sketch065
  ArcFitTolerance = 1e-06
  AttachmentSupport = -> [Pocket023]
  FullyConstrained = true
  MakeInternals = false
  MapMode = 5
  Placement = pos=(76.55,-6.858,7.62) rot=(0,-1,0;1.5708rad)
  sketch-geometry (2):
    g0: Circle CenterX=83.455 CenterY=-10.227 CenterZ=0 NormalX=0 NormalY=0 NormalZ=1 AngleXU=0 Radius=1.524
    g1: Circle CenterX=83.455 CenterY=138.243 CenterZ=0 NormalX=0 NormalY=0 NormalZ=1 AngleXU=0 Radius=1.524
  constraints (4):
    c: Coincident(g0,g-4)
    c: Equal(g0,g-4)
    c: Coincident(g1,g-3)
    c: Equal(g1,g-3)
FEATURE [PartDesign::Plane] DatumPlane043  label="front panel pane"
  AttachmentSupport = -> [Pad003]
  Length = 150.095
  MapMode = 5
  Placement = pos=(90.2009,-6.858,7.62) rot=(0.707107,0,0.707107;3.14159rad)
  ResizeMode = 0
  Width = 192.491
FEATURE [Sketcher::SketchObject] Sketch095
  ArcFitTolerance = 1e-06
  AttachmentSupport = -> [DatumPlane043]
  FullyConstrained = false
  MakeInternals = false
  MapMode = 5
  Placement = pos=(90.2009,-6.858,7.62) rot=(0.707107,0,0.707107;3.14159rad)
  sketch-geometry (4):
    g0: LineSegment StartX=-42.1465 StartY=40.6349 StartZ=0 EndX=-42.1465 EndY=-192.207 EndZ=0
    g1: LineSegment StartX=-42.1465 StartY=-192.207 StartZ=0 EndX=106.518 EndY=-192.207 EndZ=0
    g2: LineSegment StartX=106.518 StartY=-192.207 StartZ=0 EndX=106.518 EndY=40.6349 EndZ=0
    g3: LineSegment StartX=106.518 StartY=40.6349 StartZ=0 EndX=-42.1465 EndY=40.6349 EndZ=0
  constraints (8):
    c: Coincident(g0,g1)
    c: Coincident(g1,g2)
    c: Coincident(g2,g3)
    c: Coincident(g3,g0)
    c: Vertical(g0)
    c: Vertical(g2)
    c: Horizontal(g1)
    c: Horizontal(g3)
FEATURE [PartDesign::SubShapeBinder] Binder021
  BindCopyOnChange = 0
  BindMode = 0
  ClaimChildren = false
  Context = -> Part001 [Body001.Binder021.]
  Fuse = false
  MakeFace = true
  OffsetFill = false
  OffsetIntersection = false
  OffsetJoinType = 0
  OffsetOpenResult = false
  PartialLoad = false
  Refine = true
  Relative = true
  Support = -> [Part004[Body004.SubtractivePipe005.]]
  _Version = 2
FEATURE [Sketcher::SketchObject] Sketch136
  ArcFitTolerance = 1e-06
  AttachmentSupport = -> [DatumPlane043]
  ExternalGeometry = -> [Binder021]
  FullyConstrained = true
  MakeInternals = false
  MapMode = 5
  Placement = pos=(90.2009,-6.858,7.62) rot=(0.707107,0,0.707107;3.14159rad)
  sketch-geometry (6):
    g0: Circle CenterX=-12.3292 CenterY=-74.008 CenterZ=0 NormalX=0 NormalY=0 NormalZ=1 AngleXU=0 Radius=1.25
    g1: Circle CenterX=0.18542 CenterY=-74.008 CenterZ=0 NormalX=0 NormalY=0 NormalZ=1 AngleXU=0 Radius=1.25
    g2: Circle CenterX=-12.3292 CenterY=-83.8403 CenterZ=0 NormalX=0 NormalY=0 NormalZ=1 AngleXU=0 Radius=1.25
    g3: Circle CenterX=12.7 CenterY=-74.008 CenterZ=0 NormalX=0 NormalY=0 NormalZ=1 AngleXU=0 Radius=1.25
    g4: Circle CenterX=12.7 CenterY=-83.8403 CenterZ=0 NormalX=0 NormalY=0 NormalZ=1 AngleXU=0 Radius=1.25
    g5: Circle CenterX=0.18542 CenterY=-83.8403 CenterZ=0 NormalX=0 NormalY=0 NormalZ=1 AngleXU=0 Radius=1.25
  constraints (12):
    c: Coincident(g0,g-3)
    c: Coincident(g1,g-6)
    c: Coincident(g2,g-4)
    c: Coincident(g3,g-5)
    c: Coincident(g4,g-8)
    c: Coincident(g5,g-7)
    c: Equal(g5,g4)
    c: Equal(g5,g1)
    c: Equal(g5,g3)
    c: Equal(g5,g0)
    c: Equal(g2,g5)
    c: Diameter(g0) = 2.5
FEATURE [PartDesign::Pocket] Pocket043  label="LED holes"
  BaseFeature = -> Pocket023
  Direction = (-1,0,2e-16)
  Length = 2.54
  Length2 = 5
  Placement = pos=(88.5499,-6.858,7.62) rot=(0.707107,0,0.707107;3.14159rad)
  Profile = -> Sketch136
  ReferenceAxis = -> Sketch136 [N_Axis]
  Refine = true
  Suppressed = false
  TaperAngle = 15
  Type = 0
FEATURE [PartDesign::Pocket] Pocket024  label="screw holes"
  BaseFeature = -> Pocket043
  Direction = (1,0,-2e-16)
  Length = 7.874
  Length2 = 5
  Placement = pos=(88.5499,-6.858,7.62) rot=(0.707107,0,0.707107;3.14159rad)
  Profile = -> Sketch065
  ReferenceAxis = -> Sketch065 [N_Axis]
  Refine = true
  Suppressed = false
  Type = 0
FEATURE [PartDesign::Pocket] Pocket026  label="nut slots"
  BaseFeature = -> Pocket024
  Direction = (1.2e-15,0,-1)
  Length = 10.16
  Length2 = 5
  Offset = -1.27
  Placement = pos=(88.5499,-6.858,7.62) rot=(0.707107,0,0.707107;3.14159rad)
  Profile = -> Sketch067
  ReferenceAxis = -> Sketch067 [N_Axis]
  Refine = true
  Suppressed = false
  Type = 0
FEATURE [Sketcher::SketchObject] Sketch070
  ArcFitTolerance = 1e-06
  AttachmentSupport = -> [Pocket026]
  ExternalGeometry = -> [Pocket026]
  FullyConstrained = true
  MakeInternals = false
  MapMode = 5
  Placement = pos=(90.2009,-6.858,7.62) rot=(0.707107,0,0.707107;3.14159rad)
  sketch-geometry (12):
    g0: LineSegment StartX=17.256 StartY=15.942 StartZ=0 EndX=17.256 EndY=-55.312 EndZ=0
    g1: LineSegment StartX=17.256 StartY=-55.312 StartZ=0 EndX=44.264 EndY=-55.312 EndZ=0
    g2: LineSegment StartX=44.264 StartY=-55.312 StartZ=0 EndX=44.264 EndY=15.942 EndZ=0
    g3: LineSegment StartX=44.264 StartY=15.942 StartZ=0 EndX=17.256 EndY=15.942 EndZ=0
    g4: LineSegment StartX=17.256 StartY=-143.958 StartZ=0 EndX=44.264 EndY=-143.958 EndZ=0
    g5: LineSegment StartX=44.264 StartY=-143.958 StartZ=0 EndX=44.264 EndY=-72.704 EndZ=0
    g6: LineSegment StartX=44.264 StartY=-72.704 StartZ=0 EndX=17.256 EndY=-72.704 EndZ=0
    g7: LineSegment StartX=17.256 StartY=-72.704 StartZ=0 EndX=17.256 EndY=-143.958 EndZ=0
    g8: Circle CenterX=26.764 CenterY=-19.685 CenterZ=0 NormalX=0 NormalY=0 NormalZ=1 AngleXU=0 Radius=2.9972
    g9: Circle CenterX=26.764 CenterY=-108.331 CenterZ=0 NormalX=0 NormalY=0 NormalZ=1 AngleXU=0 Radius=2.9972
    g10: GeomPoint X=44.264 Y=-19.685 Z=0
    g11: GeomPoint X=44.264 Y=-108.331 Z=0
  constraints (30):
    c: Coincident(g0,g1)
    c: Coincident(g1,g2)
    c: Coincident(g2,g3)
    c: Coincident(g3,g0)
    c: Vertical(g0)
    c: Vertical(g2)
    c: Horizontal(g1)
    c: Horizontal(g3)
    c: Coincident(g0,g-5)
    c: Coincident(g4,g5)
    c: Coincident(g5,g6)
    c: Coincident(g6,g7)
    c: Coincident(g7,g4)
    c: Horizontal(g4)
    c: Horizontal(g6)
    c: Vertical(g5)
    c: Vertical(g7)
    c: Coincident(g4,g-6)
    c: PointOnObject(g-3,g1)
    c: PointOnObject(g-4,g6)
    c: Equal(g3,g4)
    c: DistanceX(g2,g-3) = 35
    c: Equal(g8,g9)
    c: Vertical(g8,g9)
    c: Symmetric(g2,g2,g10)
    c: Symmetric(g5,g5,g11)
    c: Horizontal(g10,g8)
    c: Horizontal(g11,g9)
    c: DistanceX(g8,g-3) = 52.5
    c: Diameter(g8) = 5.9944
FEATURE [PartDesign::Pad] Pad022  label="cover meter bottoms"
  BaseFeature = -> Pocket026
  Direction = (1,0,-2e-16)
  Length = 1.397
  Length2 = 10
  Placement = pos=(88.5499,-6.858,7.62) rot=(0.707107,0,0.707107;3.14159rad)
  Profile = -> Sketch070
  ReferenceAxis = -> Sketch070 [N_Axis]
  Refine = true
  Reversed = true
  Suppressed = false
  Type = 0
FEATURE [PartDesign::Pocket] Pocket006  label="hold time label"
  BaseFeature = -> Pad022
  Direction = (-1,0,2e-16)
  Length = 5
  Length2 = 5
  Placement = pos=(88.5499,-6.858,7.62) rot=(0.707107,0,0.707107;3.14159rad)
  Profile = -> Sketch022
  ReferenceAxis = -> Sketch022 [N_Axis]
  Refine = true
  Reversed = true
  Suppressed = false
  Type = 1
FEATURE [PartDesign::Pocket] Pocket034  label="clip (2)"
  BaseFeature = -> Pocket006
  Direction = (-1,0,2e-16)
  Length = 5
  Length2 = 5
  Placement = pos=(88.5499,-6.858,7.62) rot=(0.707107,0,0.707107;3.14159rad)
  Profile = -> Sketch095
  ReferenceAxis = -> Sketch095 [N_Axis]
  Refine = true
  Reversed = true
  Suppressed = false
  Type = 1
FEATURE [PartDesign::SubShapeBinder] Binder022
  BindCopyOnChange = 0
  BindMode = 0
  ClaimChildren = false
  Context = -> Part001 [Body008.Binder022.]
  Fuse = false
  MakeFace = true
  OffsetFill = false
  OffsetIntersection = false
  OffsetJoinType = 0
  OffsetOpenResult = false
  PartialLoad = false
  Refine = true
  Relative = true
  Support = -> [Body001]
  _Version = 2
FEATURE [PartDesign::Plane] DatumPlane060
  AttachmentSupport = -> [Binder022]
  Length = 238.396
  MapMode = 5
  Placement = pos=(76.55,0,0) rot=(0.57735,-0.57735,-0.57735;2.0944rad)
  ResizeMode = 0
  Width = 163.884
FEATURE [PartDesign::Body] Body001  label="front panel body"
  AllowCompound = false
  Group = -> [Binder021,Binder004,Binder005,DatumPlane002,Binder006,Sketch004,Pad002,Sketch005,DatumPlane040,Pad003,Binder007,Sketch026,DatumPlane043,Pad005,Fillet,Sketch023,Pocket007,Sketch024,Pocket008,Sketch066,Pocket025,Sketch009,Pocket004,DatumPlane003,Sketch064,Sketch136,Pocket023,Pocket043,Sketch065,Pocket024,Sketch022,DatumPlane024,Sketch067,Pocket026,Sketch070,Pad022,Pocket006,Sketch095,Pocket034,+20 more]
  Origin = -> Origin003
  Tip = -> Pad042
FEATURE [PartDesign::FeatureBase] Clone001
  BaseFeature = -> Body004
  Suppressed = false
FEATURE [PartDesign::Body] Body006  label="light pipes front panel"
  AllowCompound = false
  Group = -> [Clone001]
  Origin = -> Origin012
  Tip = -> Clone001
FEATURE [PartDesign::Plane] DatumPlane061
  AttachmentOffset = pos=(0,0,-1.016) rot=(0,0,1;0rad)
  AttachmentSupport = -> [Binder022]
  Length = 238.396
  MapMode = 5
  Placement = pos=(89.1849,-8.1e-15,-1.98e-14) rot=(0.57735,0.57735,0.57735;2.0944rad)
  ResizeMode = 0
  Width = 163.884
FEATURE [Sketcher::SketchObject] Sketch138
  ArcFitTolerance = 1e-06
  AttachmentSupport = -> [DatumPlane061]
  ExternalGeometry = -> [Binder022]
  FullyConstrained = false
  MakeInternals = false
  MapMode = 5
  Placement = pos=(89.1849,-8.1e-15,-1.98e-14) rot=(0.57735,0.57735,0.57735;2.0944rad)
  sketch-geometry (4):
    g0: LineSegment StartX=-36.5511 StartY=106.037 StartZ=0 EndX=-36.5511 EndY=-24.1934 EndZ=0
    g1: LineSegment StartX=-36.5511 StartY=-24.1934 StartZ=0 EndX=169.018 EndY=-24.1934 EndZ=0
    g2: LineSegment StartX=169.018 StartY=-24.1934 StartZ=0 EndX=169.018 EndY=106.037 EndZ=0
    g3: LineSegment StartX=169.018 StartY=106.037 StartZ=0 EndX=-36.5511 EndY=106.037 EndZ=0
  constraints (8):
    c: Coincident(g0,g1)
    c: Coincident(g1,g2)
    c: Coincident(g2,g3)
    c: Coincident(g3,g0)
    c: Vertical(g0)
    c: Vertical(g2)
    c: Horizontal(g1)
    c: Horizontal(g3)
FEATURE [PartDesign::Pad] Pad046
  Direction = (1,0,0)
  Length = 10
  Length2 = 10
  Placement = pos=(89.1849,-7.8e-15,-2e-14) rot=(0.57735,0.57735,0.57735;2.0944rad)
  Profile = -> Sketch138
  ReferenceAxis = -> Sketch138 [N_Axis]
  Refine = true
  Suppressed = false
  Type = 3
  UpToFace = -> DatumPlane060
FEATURE [PartDesign::Body] Body008  label="light pipe clip"
  AllowCompound = false
  Group = -> [Binder022,DatumPlane061,Sketch138,DatumPlane060,Pad046]
  Origin = -> Origin014
  Tip = -> Pad046
COMPONENT P3 — recipe-attached ("back panel", modeled in this document).
Construction recipe (the document's own serialized feature program — sketch geometry with constraints, then the solid features built on it; lengths are millimeters unless a unit is written):

FEATURE [PartDesign::SubShapeBinder] Binder008
  BindCopyOnChange = 0
  BindMode = 0
  ClaimChildren = false
  Context = -> Part002 [Body002.Binder008.]
  Fuse = false
  MakeFace = true
  OffsetFill = false
  OffsetIntersection = false
  OffsetJoinType = 0
  OffsetOpenResult = false
  PartialLoad = false
  Refine = true
  Relative = true
  Support = -> [Part[Body.]]
  _Version = 2
FEATURE [PartDesign::SubShapeBinder] Binder009
  BindCopyOnChange = 0
  BindMode = 0
  ClaimChildren = false
  Context = -> Part002 [Body002.Binder009.]
  Fuse = false
  MakeFace = true
  OffsetFill = false
  OffsetIntersection = false
  OffsetJoinType = 0
  OffsetOpenResult = false
  PartialLoad = false
  Refine = true
  Relative = true
  Support = -> [Link[PCB_Assembly.]]
  _Version = 2
FEATURE [PartDesign::Plane] DatumPlane007  label="PCB back plane"
  AttachmentSupport = -> [Binder009]
  Length = 178.713
  MapMode = 5
  Placement = pos=(0,0,0) rot=(0.57735,-0.57735,-0.57735;2.0944rad)
  ResizeMode = 0
  Width = 74.6328
FEATURE [Sketcher::SketchObject] Sketch031
  ArcFitTolerance = 1e-06
  AttachmentSupport = -> [DatumPlane007]
  FullyConstrained = true
  MakeInternals = false
  MapMode = 5
  Placement = pos=(0,0,0) rot=(0.57735,-0.57735,-0.57735;2.0944rad)
  sketch-geometry (4):
    g0: LineSegment StartX=-134.814 StartY=30.734 StartZ=0 EndX=-134.814 EndY=-7.366 EndZ=0
    g1: LineSegment StartX=-134.814 StartY=-7.366 StartZ=0 EndX=20.514 EndY=-7.366 EndZ=0
    g2: LineSegment StartX=20.514 StartY=-7.366 StartZ=0 EndX=20.514 EndY=30.734 EndZ=0
    g3: LineSegment StartX=20.514 StartY=30.734 StartZ=0 EndX=-134.814 EndY=30.734 EndZ=0
  constraints (12):
    c: Coincident(g0,g1)
    c: Coincident(g1,g2)
    c: Coincident(g2,g3)
    c: Coincident(g3,g0)
    c: Vertical(g0)
    c: Vertical(g2)
    c: Horizontal(g1)
    c: Horizontal(g3)
    c: DistanceX(g2,g-3) = 0.254
    c: DistanceX(g-4,g0) = 0.254
    c: DistanceY(g0,g-4) = 0.254
    c: DistanceY(g-4,g0) = 0.254
FEATURE [PartDesign::Pad] Pad010
  Direction = (-1,0,0)
  Length = 10
  Length2 = 10
  Placement = pos=(0,0,0) rot=(0.57735,-0.57735,-0.57735;2.0944rad)
  Profile = -> Sketch031
  ReferenceAxis = -> Sketch031 [N_Axis]
  Refine = true
  Suppressed = false
  Type = 3
  UpToFace = -> Binder008 [Face6]
FEATURE [PartDesign::Plane] DatumPlane008  label="PCB bottom"
  AttachmentSupport = -> [Binder009]
  Length = 67.924
  MapMode = 5
  Placement = pos=(0,0,0) rot=(1,0,0;3.14159rad)
  ResizeMode = 0
  Width = 177.719
FEATURE [Sketcher::SketchObject] Sketch032
  ArcFitTolerance = 1e-06
  AttachmentSupport = -> [DatumPlane008]
  ExternalGeometry = -> [Binder009]
  FullyConstrained = true
  MakeInternals = false
  MapMode = 5
  Placement = pos=(0,0,0) rot=(1,0,0;3.14159rad)
  sketch-geometry (6):
    g0: LineSegment StartX=0 StartY=-15.113 StartZ=0 EndX=0 EndY=-22.987 EndZ=0
    g1: LineSegment StartX=0 StartY=-22.987 StartZ=0 EndX=7.874 EndY=-22.987 EndZ=0
    g2: LineSegment StartX=7.874 StartY=-22.987 StartZ=0 EndX=7.874 EndY=-15.113 EndZ=0
    g3: Circle CenterX=3.81 CenterY=-19.05 CenterZ=0 NormalX=0 NormalY=0 NormalZ=1 AngleXU=0 Radius=1.5875
    g4: GeomPoint X=7.874 Y=-19.05 Z=0
    g5: LineSegment StartX=7.874 StartY=-15.113 StartZ=0 EndX=0 EndY=-15.113 EndZ=0
  constraints (15):
    c: Coincident(g0,g1)
    c: Coincident(g1,g2)
    c: Vertical(g0)
    c: Vertical(g2)
    c: Horizontal(g1)
    c: Diameter(g3) = 3.175
    c: DistanceY(g2,g2) = 7.874
    c: Equal(g2,g1)
    c: Symmetric(g2,g2,g4)
    c: Horizontal(g3,g4)
    c: Coincident(g5,g2)
    c: Horizontal(g5)
    c: Coincident(g5,g0)
    c: PointOnObject(g0,g-2)
    c: Coincident(g-3,g3)
FEATURE [PartDesign::Pad] Pad011
  BaseFeature = -> Pad010
  Direction = (0,0,-1)
  Length = 1.905
  Length2 = 10
  Placement = pos=(0,0,0) rot=(0.57735,-0.57735,-0.57735;2.0944rad)
  Profile = -> Sketch032
  ReferenceAxis = -> Sketch032 [N_Axis]
  Refine = true
  Suppressed = false
  Type = 0
FEATURE [Sketcher::SketchObject] Sketch033
  ArcFitTolerance = 1e-06
  AttachmentSupport = -> [DatumPlane007]
  ExternalGeometry = -> [Binder009]
  FullyConstrained = true
  MakeInternals = false
  MapMode = 5
  Placement = pos=(0,0,0) rot=(0.57735,-0.57735,-0.57735;2.0944rad)
  sketch-geometry (6):
    g0: LineSegment StartX=-44.4288 StartY=-2.794 StartZ=0 EndX=-44.4288 EndY=-6.223 EndZ=0
    g1: LineSegment StartX=-44.4288 StartY=-6.223 StartZ=0 EndX=-36.8088 EndY=-6.223 EndZ=0
    g2: LineSegment StartX=-36.8088 StartY=-6.223 StartZ=0 EndX=-36.8088 EndY=-2.794 EndZ=0
    g3: LineSegment StartX=-36.8088 StartY=-2.794 StartZ=0 EndX=-44.4288 EndY=-2.794 EndZ=0
    g4: LineSegment [constr] StartX=-44.4288 StartY=-2.794 StartZ=0 EndX=-42.2063 EndY=1.778 EndZ=0
    g5: LineSegment [constr] StartX=-39.0313 StartY=1.778 StartZ=0 EndX=-36.8088 EndY=-2.794 EndZ=0
  constraints (16):
    c: Coincident(g0,g1)
    c: Coincident(g1,g2)
    c: Coincident(g2,g3)
    c: Coincident(g3,g0)
    c: Vertical(g0)
    c: Vertical(g2)
    c: Horizontal(g1)
    c: Horizontal(g3)
    c: DistanceX(g1,g1) = 7.62
    c: DistanceY(g2,g-1) = 2.794
    c: DistanceY(g1,g2) = 3.429
    c: Coincident(g4,g0)
    c: Coincident(g4,g-4)
    c: Coincident(g5,g-4)
    c: Coincident(g5,g2)
    c: Equal(g4,g5)
FEATURE [PartDesign::Pad] Pad012
  BaseFeature = -> Pad011
  Direction = (-1,0,0)
  Length = 21.59
  Length2 = 10
  Placement = pos=(0,0,0) rot=(0.57735,-0.57735,-0.57735;2.0944rad)
  Profile = -> Sketch033
  ReferenceAxis = -> Sketch033 [N_Axis]
  Refine = true
  Reversed = true
  Suppressed = false
  Type = 0
FEATURE [Sketcher::SketchObject] Sketch035
  ArcFitTolerance = 1e-06
  AttachmentSupport = -> [Pad012]
  ExternalGeometry = -> [Binder009]
  FullyConstrained = true
  MakeInternals = false
  MapMode = 5
  Placement = pos=(-2e-16,0,-2.794) rot=(0,0,1;1.5708rad)
  sketch-geometry (1):
    g0: Circle CenterX=40.6188 CenterY=-15.24 CenterZ=0 NormalX=0 NormalY=0 NormalZ=1 AngleXU=0 Radius=1.5875
  constraints (2):
    c: Coincident(g0,g-3)
    c: Equal(g0,g-3)
FEATURE [PartDesign::Pocket] Pocket010
  BaseFeature = -> Pad012
  Direction = (0,0,-1)
  Length = 5
  Length2 = 5
  Placement = pos=(0,0,0) rot=(0.57735,-0.57735,-0.57735;2.0944rad)
  Profile = -> Sketch035
  ReferenceAxis = -> Sketch035 [N_Axis]
  Refine = true
  Suppressed = false
  Type = 1
FEATURE [PartDesign::Plane] DatumPlane009  label="clear PCB bottom connections"
  AttachmentSupport = -> [Pocket010]
  Length = 177.719
  MapMode = 5
  Placement = pos=(-2e-16,0,-2.794) rot=(0,0,1;1.5708rad)
  ResizeMode = 0
  Width = 67.924
FEATURE [PartDesign::Plane] DatumPlane010  label="boss to PCB bottom mount"
  AttachmentSupport = -> [Pocket010]
  Length = 66.3167
  MapMode = 5
  Placement = pos=(0,44.4288,-2.7e-15) rot=(0.57735,-0.57735,-0.57735;4.18879rad)
  ResizeMode = 0
  Width = 60.6016
FEATURE [Sketcher::SketchObject] Sketch036
  ArcFitTolerance = 1e-06
  AttachmentSupport = -> [DatumPlane010]
  ExternalGeometry = -> [Binder009,Pocket010]
  FullyConstrained = false
  MakeInternals = false
  MapMode = 5
  Placement = pos=(0,44.4288,-2.7e-15) rot=(0.57735,-0.57735,-0.57735;4.18879rad)
  sketch-geometry (4):
    g0: LineSegment StartX=2.794 StartY=-21.59 StartZ=0 EndX=-2.7e-15 EndY=-21.59 EndZ=0
    g1: LineSegment StartX=-2.7e-15 StartY=-21.59 StartZ=0 EndX=0 EndY=-12.0856 EndZ=0
    g2: LineSegment StartX=0 StartY=-12.0856 StartZ=0 EndX=2.794 EndY=-10.795 EndZ=0
    g3: LineSegment StartX=2.794 StartY=-10.795 StartZ=0 EndX=2.794 EndY=-21.59 EndZ=0
  constraints (9):
    c: Coincident(g0,g-4)
    c: PointOnObject(g0,g-3)
    c: Horizontal(g0)
    c: Coincident(g1,g0)
    c: PointOnObject(g1,g-3)
    c: Coincident(g2,g1)
    c: Symmetric(g-4,g-4,g2)
    c: Coincident(g3,g2)
    c: Coincident(g3,g0)
FEATURE [PartDesign::Pad] Pad013
  BaseFeature = -> Pocket010
  Direction = (0,1,0)
  Length = 10
  Length2 = 10
  Placement = pos=(0,0,0) rot=(0.57735,-0.57735,-0.57735;2.0944rad)
  Profile = -> Sketch036
  ReferenceAxis = -> Sketch036 [N_Axis]
  Refine = true
  Suppressed = false
  Type = 3
  UpToFace = -> Pocket010 [Face8]
FEATURE [Sketcher::SketchObject] Sketch037
  ArcFitTolerance = 1e-06
  AttachmentSupport = -> [DatumPlane009]
  ExternalGeometry = -> [Pad013]
  FullyConstrained = true
  MakeInternals = false
  MapMode = 5
  Placement = pos=(-2e-16,0,-2.794) rot=(0,0,1;1.5708rad)
  sketch-geometry (1):
    g0: Circle CenterX=40.6188 CenterY=-15.24 CenterZ=0 NormalX=0 NormalY=0 NormalZ=1 AngleXU=0 Radius=1.5875
  constraints (2):
    c: Coincident(g0,g-3)
    c: Equal(g0,g-3)
FEATURE [PartDesign::Pocket] Pocket011
  BaseFeature = -> Pad013
  Direction = (0,0,-1)
  Length = 5
  Length2 = 5
  Midplane = true
  Placement = pos=(0,0,0) rot=(0.57735,-0.57735,-0.57735;2.0944rad)
  Profile = -> Sketch037
  ReferenceAxis = -> Sketch037 [N_Axis]
  Refine = true
  Suppressed = false
  Type = 1
FEATURE [PartDesign::Plane] DatumPlane014  label="sub panel boss interface"
  AttachmentSupport = -> [Binder008]
  Length = 67.924
  MapMode = 5
  Placement = pos=(1.71e-14,-1.1e-15,-5.08) rot=(0,0,1;0rad)
  ResizeMode = 0
  Width = 177.719
FEATURE [Sketcher::SketchObject] Sketch042
  ArcFitTolerance = 1e-06
  AttachmentSupport = -> [DatumPlane014]
  ExternalGeometry = -> [Pocket011]
  FullyConstrained = true
  MakeInternals = false
  MapMode = 5
  Placement = pos=(1.71e-14,-1.1e-15,-5.08) rot=(0,0,1;0rad)
  sketch-geometry (12):
    g0: Circle CenterX=11.049 CenterY=110.49 CenterZ=0 NormalX=0 NormalY=0 NormalZ=1 AngleXU=0 Radius=1.905
    g1: Circle CenterX=11.049 CenterY=-8.89 CenterZ=0 NormalX=0 NormalY=0 NormalZ=1 AngleXU=0 Radius=1.905
    g2: LineSegment StartX=-1.651 StartY=120.396 StartZ=0 EndX=-1.651 EndY=100.584 EndZ=0
    g3: LineSegment StartX=-1.651 StartY=100.584 StartZ=0 EndX=19.939 EndY=100.584 EndZ=0
    g4: LineSegment StartX=19.939 StartY=100.584 StartZ=0 EndX=19.939 EndY=120.396 EndZ=0
    g5: LineSegment StartX=19.939 StartY=120.396 StartZ=0 EndX=-1.651 EndY=120.396 EndZ=0
    g6: LineSegment StartX=19.939 StartY=-18.796 StartZ=0 EndX=19.939 EndY=1.016 EndZ=0
    g7: LineSegment StartX=19.939 StartY=1.016 StartZ=0 EndX=-1.651 EndY=1.016 EndZ=0
    g8: LineSegment StartX=-1.651 StartY=1.016 StartZ=0 EndX=-1.651 EndY=-18.796 EndZ=0
    g9: LineSegment StartX=-1.651 StartY=-18.796 StartZ=0 EndX=19.939 EndY=-18.796 EndZ=0
    g10: GeomPoint X=19.939 Y=110.49 Z=0
    g11: GeomPoint X=19.939 Y=-8.89 Z=0
  constraints (30):
    c: Coincident(g0,g-3)
    c: Equal(g0,g-3)
    c: Coincident(g1,g-8)
    c: Equal(g1,g-8)
    c: Coincident(g2,g3)
    c: Coincident(g3,g4)
    c: Coincident(g4,g5)
    c: Coincident(g5,g2)
    c: Vertical(g2)
    c: Vertical(g4)
    c: Horizontal(g3)
    c: Horizontal(g5)
    c: Coincident(g6,g7)
    c: Coincident(g7,g8)
    c: Coincident(g8,g9)
    c: Coincident(g9,g6)
    c: Vertical(g6)
    c: Vertical(g8)
    c: Horizontal(g7)
    c: Horizontal(g9)
    c: Symmetric(g4,g4,g10)
    c: Symmetric(g6,g6,g11)
    c: Horizontal(g1,g11)
    c: Horizontal(g10,g0)
    c: Equal(g4,g6)
    c: Vertical(g-9,g2)
    c: Vertical(g-9,g7)
    c: DistanceX(g-5,g4) = 2.54
    c: Equal(g3,g7)
    c: DistanceY(g6,g-6) = 3.556
FEATURE [PartDesign::Pad] Pad016
  BaseFeature = -> Pocket011
  Direction = (-3.4e-15,0,1)
  Length = 4.826
  Length2 = 10
  Placement = pos=(0,0,0) rot=(0.57735,-0.57735,-0.57735;2.0944rad)
  Profile = -> Sketch042
  ReferenceAxis = -> Sketch042 [N_Axis]
  Refine = true
  Suppressed = false
  Type = 0
FEATURE [PartDesign::Plane] DatumPlane015  label="Boss to subpanel top"
  AttachmentSupport = -> [Pad016]
  Length = 177.719
  MapMode = 5
  Placement = pos=(8e-16,0,-0.254) rot=(0,0,1;1.5708rad)
  ResizeMode = 0
  Width = 67.924
FEATURE [Sketcher::SketchObject] Sketch043
  ArcFitTolerance = 1e-06
  AttachmentSupport = -> [DatumPlane015]
  ExternalGeometry = -> [Pad016]
  FullyConstrained = true
  MakeInternals = false
  MapMode = 5
  Placement = pos=(8e-16,0,-0.254) rot=(0,0,1;1.5708rad)
  sketch-geometry (14):
    g0: LineSegment StartX=-4.9149 StartY=-8.75397 StartZ=0 EndX=-8.89 EndY=-6.45895 EndZ=0
    g1: LineSegment StartX=-8.89 StartY=-6.45895 StartZ=0 EndX=-12.8651 EndY=-8.75397 EndZ=0
    g2: LineSegment StartX=-12.8651 StartY=-8.75397 StartZ=0 EndX=-12.8651 EndY=-13.344 EndZ=0
    g3: LineSegment StartX=-12.8651 StartY=-13.344 StartZ=0 EndX=-8.89 EndY=-15.6391 EndZ=0
    g4: LineSegment StartX=-8.89 StartY=-15.6391 StartZ=0 EndX=-4.9149 EndY=-13.344 EndZ=0
    g5: LineSegment StartX=-4.9149 StartY=-13.344 StartZ=0 EndX=-4.9149 EndY=-8.75397 EndZ=0
    g6: Circle [constr] CenterX=-8.89 CenterY=-11.049 CenterZ=0 NormalX=0 NormalY=0 NormalZ=1 AngleXU=0 Radius=4.59005
    g7: LineSegment StartX=110.49 StartY=-6.45895 StartZ=0 EndX=106.515 EndY=-8.75397 EndZ=0
    g8: LineSegment StartX=106.515 StartY=-8.75397 StartZ=0 EndX=106.515 EndY=-13.344 EndZ=0
    g9: LineSegment StartX=106.515 StartY=-13.344 StartZ=0 EndX=110.49 EndY=-15.6391 EndZ=0
    g10: LineSegment StartX=110.49 StartY=-15.6391 StartZ=0 EndX=114.465 EndY=-13.344 EndZ=0
    g11: LineSegment StartX=114.465 StartY=-13.344 StartZ=0 EndX=114.465 EndY=-8.75397 EndZ=0
    g12: LineSegment StartX=114.465 StartY=-8.75397 StartZ=0 EndX=110.49 EndY=-6.45895 EndZ=0
    g13: Circle [constr] CenterX=110.49 CenterY=-11.049 CenterZ=0 NormalX=0 NormalY=0 NormalZ=1 AngleXU=0 Radius=4.59005
  constraints (32):
    c: Coincident(g0,g1)
    c: Coincident(g1,g2)
    c: Coincident(g2,g3)
    c: Coincident(g3,g4)
    c: Coincident(g4,g5)
    c: Coincident(g5,g0)
    c: Equal(g0, g1-g5) x5
    c: PointOnObject(g0,g6)
    c: PointOnObject(g1,g6)
    c: PointOnObject(g2,g6)
    c: PointOnObject(g3,g6)
    c: PointOnObject(g4,g6)
    c: PointOnObject(g5,g6)
    c: Coincident(g6,g-4)
    c: Distance(g0,g2) = 7.9502
    c: Coincident(g7,g8)
    c: Coincident(g8,g9)
    c: Coincident(g9,g10)
    c: Coincident(g10,g11)
    c: Coincident(g11,g12)
    c: Coincident(g12,g7)
    c: Equal(g7, g8-g12) x5
    c: PointOnObject(g7,g13)
    c: PointOnObject(g8,g13)
    c: PointOnObject(g9,g13)
    c: PointOnObject(g10,g13)
    c: PointOnObject(g11,g13)
    c: PointOnObject(g12,g13)
    c: Coincident(g13,g-3)
    c: Equal(g12,g1)
    c: Vertical(g5)
    c: Vertical(g11)
FEATURE [PartDesign::Plane] DatumPlane022  label="lid top001"
  AttachmentSupport = -> [Binder008]
  Length = 181.716
  MapMode = 5
  Placement = pos=(-15.4593,8.3e-15,14.4583) rot=(0.369852,-0.369852,-0.852302;1.72994rad)
  ResizeMode = 0
  Width = 96.7815
FEATURE [Sketcher::SketchObject] Sketch051
  ArcFitTolerance = 1e-06
  AttachmentSupport = -> [DatumPlane022]
  FullyConstrained = false
  MakeInternals = false
  MapMode = 5
  Placement = pos=(-15.4593,8.3e-15,14.4583) rot=(0.369852,-0.369852,-0.852302;1.72994rad)
  sketch-geometry (4):
    g0: LineSegment StartX=-148.189 StartY=30.2491 StartZ=0 EndX=-148.189 EndY=11.5316 EndZ=0
    g1: LineSegment StartX=-148.189 StartY=11.5316 StartZ=0 EndX=46.1544 EndY=11.5316 EndZ=0
    g2: LineSegment StartX=46.1544 StartY=11.5316 StartZ=0 EndX=46.1544 EndY=30.2491 EndZ=0
    g3: LineSegment StartX=46.1544 StartY=30.2491 StartZ=0 EndX=-148.189 EndY=30.2491 EndZ=0
  constraints (8):
    c: Coincident(g0,g1)
    c: Coincident(g1,g2)
    c: Coincident(g2,g3)
    c: Coincident(g3,g0)
    c: Vertical(g0)
    c: Vertical(g2)
    c: Horizontal(g1)
    c: Horizontal(g3)
FEATURE [PartDesign::Pocket] Pocket020
  BaseFeature = -> Pad016
  Direction = (0.730358,0,-0.683065)
  Length = 5
  Length2 = 5
  Placement = pos=(0,0,0) rot=(0.57735,-0.57735,-0.57735;2.0944rad)
  Profile = -> Sketch051
  ReferenceAxis = -> Sketch051 [N_Axis]
  Refine = true
  Reversed = true
  Suppressed = false
  Type = 1
FEATURE [PartDesign::SubShapeBinder] Binder012  label="coupler"
  BindCopyOnChange = 0
  BindMode = 0
  ClaimChildren = false
  Context = -> Part002 [Body002.Binder012.]
  Fuse = false
  MakeFace = true
  OffsetFill = false
  OffsetIntersection = false
  OffsetJoinType = 0
  OffsetOpenResult = false
  PartialLoad = false
  Refine = true
  Relative = true
  Support = -> [Link002]
  _Version = 2
FEATURE [Sketcher::SketchObject] Sketch052
  ArcFitTolerance = 1e-06
  AttachmentSupport = -> [Pocket020]
  ExternalGeometry = -> [Binder009,Binder012]
  FullyConstrained = false
  MakeInternals = false
  MapMode = 5
  Placement = pos=(-1.651,0,1e-16) rot=(0.57735,-0.57735,-0.57735;2.0944rad)
  sketch-geometry (36):
    g0: LineSegment StartX=-39.664 StartY=5.65043 StartZ=0 EndX=-39.664 EndY=1.89949 EndZ=0
    g1: LineSegment StartX=-39.664 StartY=1.89949 StartZ=0 EndX=-34.448 EndY=1.89949 EndZ=0
    g2: LineSegment StartX=-34.448 StartY=1.89949 StartZ=0 EndX=-34.448 EndY=5.65043 EndZ=0
    g3: LineSegment StartX=-34.448 StartY=5.65043 StartZ=0 EndX=-39.664 EndY=5.65043 EndZ=0
    g4: LineSegment StartX=-47.148 StartY=5.65043 StartZ=0 EndX=-52.364 EndY=5.65043 EndZ=0
    g5: LineSegment StartX=-52.364 StartY=5.65043 StartZ=0 EndX=-52.364 EndY=1.89949 EndZ=0
    g6: LineSegment StartX=-52.364 StartY=1.89949 StartZ=0 EndX=-47.148 EndY=1.89949 EndZ=0
    g7: LineSegment StartX=-47.148 StartY=1.89949 StartZ=0 EndX=-47.148 EndY=5.65043 EndZ=0
    g8: LineSegment [constr] StartX=-47.656 StartY=3.77496 StartZ=0 EndX=-47.148 EndY=3.77496 EndZ=0
    g9: LineSegment [constr] StartX=-51.856 StartY=2.40749 StartZ=0 EndX=-47.656 EndY=2.40749 EndZ=0
    g10: LineSegment [constr] StartX=-49.756 StartY=2.40749 StartZ=0 EndX=-49.756 EndY=1.89949 EndZ=0
    g11: LineSegment [constr] StartX=-34.956 StartY=3.77496 StartZ=0 EndX=-34.448 EndY=3.77496 EndZ=0
    g12: LineSegment [constr] StartX=-39.156 StartY=2.40749 StartZ=0 EndX=-34.956 EndY=2.40749 EndZ=0
    g13: LineSegment [constr] StartX=-37.056 StartY=2.40749 StartZ=0 EndX=-37.056 EndY=1.89949 EndZ=0
    g14: Circle CenterX=-91.9586 CenterY=22.028 CenterZ=0 NormalX=0 NormalY=0 NormalZ=1 AngleXU=0 Radius=5.08
    g15: Circle CenterX=-91.9586 CenterY=8.028 CenterZ=0 NormalX=0 NormalY=0 NormalZ=1 AngleXU=0 Radius=5.08
    g16: Circle CenterX=-82.9586 CenterY=15.028 CenterZ=0 NormalX=0 NormalY=0 NormalZ=1 AngleXU=0 Radius=1.651
    g17: LineSegment StartX=-70.794 StartY=13.032 StartZ=0 EndX=-70.794 EndY=1.524 EndZ=0
    g18: LineSegment StartX=-70.794 StartY=1.524 StartZ=0 EndX=-61.286 EndY=1.524 EndZ=0
    g19: LineSegment StartX=-61.286 StartY=1.524 StartZ=0 EndX=-61.286 EndY=13.032 EndZ=0
    g20: LineSegment StartX=-61.286 StartY=13.032 StartZ=0 EndX=-70.794 EndY=13.032 EndZ=0
    g21: LineSegment [constr] StartX=-70.54 StartY=12.778 StartZ=0 EndX=-61.54 EndY=12.778 EndZ=0
    g22: LineSegment [constr] StartX=-66.04 StartY=13.032 StartZ=0 EndX=-66.04 EndY=12.778 EndZ=0
    g23: LineSegment [constr] StartX=-70.54 StartY=7.278 StartZ=0 EndX=-70.794 EndY=7.278 EndZ=0
    g24: ArcOfCircle CenterX=-18.355 CenterY=15.544 CenterZ=0 NormalX=0 NormalY=0 NormalZ=1 AngleXU=0 Radius=1.7145 StartAngle=1.5708 EndAngle=3.14159
    g25: ArcOfCircle CenterX=-18.355 CenterY=14.984 CenterZ=0 NormalX=0 NormalY=0 NormalZ=1 AngleXU=0 Radius=1.7145 StartAngle=3.14159 EndAngle=4.71239
    g26: ArcOfCircle CenterX=-12.015 CenterY=15.544 CenterZ=0 NormalX=0 NormalY=0 NormalZ=1 AngleXU=0 Radius=1.7145 StartAngle=6e-16 EndAngle=1.5708
    g27: ArcOfCircle CenterX=-12.015 CenterY=14.984 CenterZ=0 NormalX=0 NormalY=0 NormalZ=1 AngleXU=0 Radius=1.7145 StartAngle=4.71239 EndAngle=6.28319
    g28: LineSegment StartX=-18.355 StartY=17.2585 StartZ=0 EndX=-12.015 EndY=17.2585 EndZ=0
    g29: LineSegment StartX=-20.0695 StartY=15.544 StartZ=0 EndX=-20.0695 EndY=14.984 EndZ=0
    g30: LineSegment StartX=-18.355 StartY=13.2695 StartZ=0 EndX=-12.015 EndY=13.2695 EndZ=0
    g31: LineSegment StartX=-10.3005 StartY=15.544 StartZ=0 EndX=-10.3005 EndY=14.984 EndZ=0
    g32: ArcOfCircle CenterX=7.62 CenterY=15.24 CenterZ=0 NormalX=0 NormalY=0 NormalZ=1 AngleXU=0 Radius=8.05 StartAngle=2.10315 EndAngle=7.32163
    g33: ArcOfCircle CenterX=-11.6417 CenterY=4.728 CenterZ=0 NormalX=0 NormalY=0 NormalZ=1 AngleXU=0 Radius=2.54 StartAngle=0.872857 EndAngle=7.15604
    g34: LineSegment StartX=3.53412 StartY=22.176 StartZ=0 EndX=11.7059 EndY=22.176 EndZ=0
    g35: LineSegment [constr] StartX=7.62 StartY=22.176 StartZ=0 EndX=7.62 EndY=7.19 EndZ=0
  constraints (88):
    c: Coincident(g32,g-13)
    c: Coincident(g33,g-10)
    c: Coincident(g0,g1)
    c: Coincident(g1,g2)
    c: Coincident(g2,g3)
    c: Coincident(g3,g0)
    c: Vertical(g0)
    c: Vertical(g2)
    c: Horizontal(g1)
    c: Horizontal(g3)
    c: Coincident(g4,g5)
    c: Coincident(g5,g6)
    c: Coincident(g6,g7)
    c: Coincident(g7,g4)
    c: Horizontal(g4)
    c: Horizontal(g6)
    c: Vertical(g5)
    c: Vertical(g7)
    c: Symmetric(g-11,g-11,g8)
    c: Symmetric(g7,g7,g8)
    c: Coincident(g9,g-12)
    c: Coincident(g9,g-11)
    c: Symmetric(g9,g9,g10)
    c: Symmetric(g6,g6,g10)
    c: Symmetric(g-8,g-8,g11)
    c: Symmetric(g2,g2,g11)
    c: Coincident(g12,g-9)
    c: Coincident(g12,g-8)
    c: Symmetric(g12,g12,g13)
    c: Symmetric(g1,g1,g13)
    c: Horizontal(g8)
    c: Horizontal(g11)
    c: Vertical(g10)
    c: Vertical(g13)
    c: Equal(g10,g8)
    c: Equal(g8,g13)
    c: Equal(g13,g11)
    c: DistanceX(g11,g11) = 0.508
    c: Coincident(g14,g-5)
    c: Coincident(g15,g-6)
    c: Equal(g15,g14)
    c: Diameter(g15) = 10.16
    c: Coincident(g16,g-7)
    c: Diameter(g16) = 3.302
    c: Coincident(g17,g18)
    c: Coincident(g18,g19)
    c: Coincident(g19,g20)
    c: Coincident(g20,g17)
    c: Vertical(g17)
    c: Vertical(g19)
    c: Horizontal(g18)
    c: Horizontal(g20)
    c: Coincident(g21,g-3)
    c: Coincident(g21,g-4)
    c: Symmetric(g20,g20,g22)
    c: Symmetric(g21,g21,g22)
    c: Symmetric(g-3,g-3,g23)
    c: Symmetric(g17,g17,g23)
    c: Horizontal(g23)
    c: Vertical(g22)
    c: Equal(g23,g22)
    c: DistanceY(g22,g22) = 0.254
    c: Coincident(g24,g-15)
    c: Coincident(g25,g-16)
    c: Coincident(g26,g-14)
    c: Coincident(g27,g-17)
    c: Equal(g26,g27)
    c: Equal(g26,g24)
    c: Equal(g24,g25)
    c: Diameter(g24) = 3.429
    c: Tangent(g24,g28) = 1.5708
    c: Tangent(g25,g30) = -1.5708
    c: Tangent(g24,g29) = -1.5708
    c: Tangent(g25,g29) = -1.5708
    c: Tangent(g27,g30) = -1.5708
    c: Tangent(g26,g28) = 1.5708
    c: Tangent(g26,g31) = 1.5708
    c: Tangent(g27,g31) = 1.5708
    c: Diameter(g32) = 16.1
    c: Diameter(g33) = 5.08
    c: Horizontal(g34)
    c: Coincident(g32,g34)
    c: Coincident(g32,g34)
    c: PointOnObject(g35,g34)
    c: PointOnObject(g35,g32)
    c: Vertical(g35)
    c: PointOnObject(g32,g35)
    c: DistanceY(g35,g35) = 14.986
FEATURE [PartDesign::Pocket] Pocket021  label="back panel holes"
  BaseFeature = -> Pocket020
  Direction = (1,-2.2e-15,0)
  Length = 5
  Length2 = 5
  Placement = pos=(0,0,0) rot=(0.57735,-0.57735,-0.57735;2.0944rad)
  Profile = -> Sketch052
  ReferenceAxis = -> Sketch052 [N_Axis]
  Refine = true
  Suppressed = false
  Type = 2
FEATURE [PartDesign::Plane] DatumPlane023  label="text extrude plane"
  AttachmentOffset = pos=(0,0,-1) rot=(0,0,1;0rad)
  AttachmentSupport = -> [Pocket021]
  Length = 178.713
  MapMode = 5
  Placement = pos=(-0.651,0,1e-16) rot=(0.57735,-0.57735,-0.57735;2.0944rad)
  ResizeMode = 0
  Width = 74.6328
FEATURE [Sketcher::SketchObject] Sketch063
  ArcFitTolerance = 1e-06
  AttachmentSupport = -> [DatumPlane023]
  FullyConstrained = true
  MakeInternals = false
  MapMode = 5
  Placement = pos=(-0.651,0,1e-16) rot=(0.57735,-0.57735,-0.57735;2.0944rad)
FEATURE [Part::Part2DObjectPython] ShapeString016  # Draft 2D object (typed FeaturePython)
  FontFile = <path>
  Fuse = false
  Justification = 6
  JustificationReference = 0
  KeepLeftMargin = false
  MakeFace = true
  ObliqueAngle = 0
  Placement = pos=(0,99.9896,9.63168) rot=(0.003016,-0.999991,-0.003016;1.57081rad)
  ScaleToSize = true
  Size = 4.318
  String = ALO
  Tracking = 0
FEATURE [Part::Part2DObjectPython] ShapeString017  # Draft 2D object (typed FeaturePython)
  FontFile = <path>
  Fuse = false
  Justification = 6
  JustificationReference = 0
  KeepLeftMargin = false
  MakeFace = true
  ObliqueAngle = 0
  Placement = pos=(-1.5e-15,71.6377,-5.45875) rot=(0.57735,-0.57735,-0.57735;2.0944rad)
  ScaleToSize = true
  Size = 4.318
  String = 12V
  Tracking = 0
FEATURE [Part::Part2DObjectPython] ShapeString018  # Draft 2D object (typed FeaturePython)
  FontFile = <path>
  Fuse = false
  Justification = 6
  JustificationReference = 0
  KeepLeftMargin = false
  MakeFace = true
  ObliqueAngle = 0
  Placement = pos=(2e-16,67.2184,23.1313) rot=(-0.575711,0.580615,0.575711;4.19368rad)
  ScaleToSize = true
  Size = 4.318
  String = POWER
  Tracking = 0
FEATURE [Part::Part2DObjectPython] ShapeString019  # Draft 2D object (typed FeaturePython)
  FontFile = <path>
  Fuse = false
  Justification = 6
  JustificationReference = 0
  KeepLeftMargin = false
  MakeFace = true
  ObliqueAngle = 0
  Placement = pos=(2e-16,41.0471,23.434) rot=(0.57735,-0.57735,-0.57735;2.0944rad)
  ScaleToSize = true
  Size = 4.318
  String = ALO
  Tracking = 0
FEATURE [PartDesign::Body] Body002
  AllowCompound = false
  Group = -> [Binder008,Binder009,DatumPlane007,Sketch031,Pad010,DatumPlane008,Sketch032,Pad011,Sketch033,Pad012,Sketch035,Pocket010,DatumPlane009,DatumPlane010,Sketch036,Pad013,Sketch037,Pocket011,DatumPlane014,Sketch042,Pad016,DatumPlane015,Sketch043,DatumPlane022,Sketch051,Pocket020,Sketch052,Binder012,Pocket021,DatumPlane023,Sketch063,ShapeString016,ShapeString017,ShapeString018,ShapeString019,+19 more]
  Origin = -> Origin005
  Tip = -> Pad035
COMPONENT P4 — recipe-attached ("lid", modeled in this document).
Construction recipe (the document's own serialized feature program — sketch geometry with constraints, then the solid features built on it; lengths are millimeters unless a unit is written):

FEATURE [PartDesign::SubShapeBinder] Binder010
  BindCopyOnChange = 0
  BindMode = 0
  ClaimChildren = false
  Context = -> Part003 [Body003.Binder010.]
  Fuse = false
  MakeFace = true
  OffsetFill = false
  OffsetIntersection = false
  OffsetJoinType = 0
  OffsetOpenResult = false
  PartialLoad = false
  Refine = true
  Relative = true
  Support = -> [Part]
  _Version = 2
FEATURE [PartDesign::SubShapeBinder] Binder011
  BindCopyOnChange = 0
  BindMode = 0
  ClaimChildren = false
  Context = -> Part003 [Body003.Binder011.]
  Fuse = false
  MakeFace = true
  OffsetFill = false
  OffsetIntersection = false
  OffsetJoinType = 0
  OffsetOpenResult = false
  PartialLoad = false
  Refine = true
  Relative = true
  Support = -> [Part002]
  _Version = 2
FEATURE [PartDesign::Plane] DatumPlane018  label="console inner right"
  AttachmentOffset = pos=(0,0,0.1016) rot=(0,0,1;0rad)
  AttachmentSupport = -> [Binder010]
  Length = 104.799
  MapMode = 5
  Placement = pos=(0,-20.6664,0) rot=(0,0.707107,0.707107;3.14159rad)
  ResizeMode = 0
  Width = 139.644
FEATURE [PartDesign::Plane] DatumPlane019  label="console inner left"
  AttachmentOffset = pos=(0,0,0.1016) rot=(0,0,1;0rad)
  AttachmentSupport = -> [Binder010]
  Length = 104.799
  MapMode = 5
  Placement = pos=(0,134.966,0) rot=(1,0,0;1.5708rad)
  ResizeMode = 0
  Width = 139.644
FEATURE [Sketcher::SketchObject] Sketch048
  ArcFitTolerance = 1e-06
  AttachmentSupport = -> [DatumPlane018]
  FullyConstrained = true
  MakeInternals = false
  MapMode = 5
  Placement = pos=(0,-20.6664,0) rot=(0,0.707107,0.707107;3.14159rad)
  sketch-geometry (10):
    g0: LineSegment StartX=-59.659 StartY=94.504 StartZ=0 EndX=-52.039 EndY=94.504 EndZ=0
    g1: LineSegment [constr] StartX=-52.039 StartY=94.504 StartZ=0 EndX=-52.039 EndY=86.63 EndZ=0
    g2: LineSegment [constr] StartX=-52.039 StartY=86.63 StartZ=0 EndX=-0.254 EndY=31.2596 EndZ=0
    g3: LineSegment StartX=-0.254 StartY=31.2596 StartZ=0 EndX=-0.254 EndY=28.6566 EndZ=0
    g4: LineSegment [constr] StartX=-0.254 StartY=28.6566 StartZ=0 EndX=-53.3376 EndY=85.4155 EndZ=0
    g5: LineSegment [constr] StartX=-53.3376 StartY=85.4155 StartZ=0 EndX=-53.3376 EndY=92.726 EndZ=0
    g6: LineSegment StartX=-53.3376 StartY=92.726 StartZ=0 EndX=-59.659 EndY=92.726 EndZ=0
    g7: LineSegment StartX=-59.659 StartY=92.726 StartZ=0 EndX=-59.659 EndY=94.504 EndZ=0
    g8: LineSegment StartX=-52.039 StartY=94.504 StartZ=0 EndX=-0.254 EndY=31.2596 EndZ=0
    g9: LineSegment StartX=-0.254 StartY=28.6566 StartZ=0 EndX=-53.3376 EndY=92.726 EndZ=0
  constraints (25):
    c: Horizontal(g0)
    c: Coincident(g1,g0)
    c: Coincident(g3,g2)
    c: Coincident(g4,g3)
    c: Coincident(g5,g4)
    c: Coincident(g6,g5)
    c: Horizontal(g6)
    c: Coincident(g7,g6)
    c: Coincident(g7,g0)
    c: Vertical(g7)
    c: Coincident(g2,g1)
    c: DistanceY(g0,g-5) = 0.254
    c: Vertical(g1)
    c: Coincident(g-3,g1)
    c: DistanceY(g6,g0) = 1.778
    c: Tangent(g4,g-4) = 1.5708
    c: Vertical(g5)
    c: DistanceX(g3,g-4) = 0.254
    c: Vertical(g3)
    c: Tangent(g2,g-3)
    c: DistanceX(g0,g0) = 7.62
    c: Coincident(g8,g0)
    c: Coincident(g8,g2)
    c: Coincident(g9,g3)
    c: Coincident(g9,g5)
FEATURE [PartDesign::Pad] Pad018
  Direction = (0,1,-2e-16)
  Length = 10
  Length2 = 10
  Placement = pos=(0,-20.6664,0) rot=(0,0.707107,0.707107;3.14159rad)
  Profile = -> Sketch048
  ReferenceAxis = -> Sketch048 [N_Axis]
  Refine = true
  Suppressed = false
  Type = 3
  UpToFace = -> DatumPlane019
FEATURE [PartDesign::Plane] DatumPlane020  label="back panel interfce"
  AttachmentSupport = -> [Pad018]
  Length = 147.179
  MapMode = 5
  Placement = pos=(0.254,-20.6664,0) rot=(0,-1,0;1.5708rad)
  ResizeMode = 0
  Width = 187.642
FEATURE [Sketcher::SketchObject] Sketch049
  ArcFitTolerance = 1e-06
  AttachmentSupport = -> [DatumPlane020]
  ExternalGeometry = -> [Pad018]
  FullyConstrained = true
  MakeInternals = false
  MapMode = 5
  Placement = pos=(0.254,-20.6664,0) rot=(0,-1,0;1.5708rad)
  sketch-geometry (4):
    g0: LineSegment StartX=31.2596 StartY=2.54 StartZ=0 EndX=31.2596 EndY=152.788 EndZ=0
    g1: LineSegment StartX=31.2596 StartY=152.788 StartZ=0 EndX=27.4496 EndY=152.788 EndZ=0
    g2: LineSegment StartX=27.4496 StartY=152.788 StartZ=0 EndX=27.4496 EndY=2.54 EndZ=0
    g3: LineSegment StartX=27.4496 StartY=2.54 StartZ=0 EndX=31.2596 EndY=2.54 EndZ=0
  constraints (11):
    c: Coincident(g0,g1)
    c: Coincident(g1,g2)
    c: Coincident(g2,g3)
    c: Coincident(g3,g0)
    c: Vertical(g2)
    c: Horizontal(g1)
    c: Horizontal(g3)
    c: DistanceY(g0,g-3) = 0.254
    c: Tangent(g-6,g0)
    c: DistanceY(g-4,g0) = 0.254
    c: DistanceX(g2,g0) = 3.81
FEATURE [PartDesign::SubShapeBinder] Binder015
  BindCopyOnChange = 0
  BindMode = 0
  ClaimChildren = false
  Context = -> Part003 [Body003.Binder015.]
  Fuse = false
  MakeFace = true
  OffsetFill = false
  OffsetIntersection = false
  OffsetJoinType = 0
  OffsetOpenResult = false
  PartialLoad = false
  Refine = true
  Relative = true
  Support = -> [Link[PCB_Assembly.]]
  _Version = 2
FEATURE [Sketcher::SketchObject] Sketch106
  ArcFitTolerance = 1e-06
  AttachmentSupport = -> [DatumPlane018]
  ExternalGeometry = -> [Pad018]
  FullyConstrained = true
  MakeInternals = false
  MapMode = 5
  Placement = pos=(0,-20.6664,0) rot=(0,0.707107,0.707107;3.14159rad)
  sketch-geometry (5):
    g0: LineSegment StartX=-52.039 StartY=94.504 StartZ=0 EndX=-53.3376 EndY=92.726 EndZ=0
    g1: LineSegment StartX=-53.3376 StartY=92.726 StartZ=0 EndX=-53.3376 EndY=85.4155 EndZ=0
    g2: LineSegment StartX=-53.3376 StartY=85.4155 StartZ=0 EndX=-0.254 EndY=28.6566 EndZ=0
    g3: LineSegment StartX=-0.254 StartY=28.6566 StartZ=0 EndX=-0.254 EndY=31.2596 EndZ=0
    g4: LineSegment StartX=-0.254 StartY=31.2596 StartZ=0 EndX=-52.039 EndY=94.504 EndZ=0
  constraints (11):
    c: Coincident(g0,g-4)
    c: Coincident(g0,g-6)
    c: Coincident(g1,g0)
    c: PointOnObject(g1,g-3)
    c: Vertical(g1)
    c: Coincident(g2,g1)
    c: Coincident(g2,g-5)
    c: Coincident(g3,g2)
    c: Coincident(g3,g-5)
    c: Coincident(g4,g3)
    c: Coincident(g4,g0)
FEATURE [PartDesign::Pad] Pad032
  BaseFeature = -> Pad018
  Direction = (0,1,-2e-16)
  Length = 1.5748
  Length2 = 10
  Placement = pos=(0,-20.6664,0) rot=(0,0.707107,0.707107;3.14159rad)
  Profile = -> Sketch106
  ReferenceAxis = -> Sketch106 [N_Axis]
  Refine = true
  Suppressed = false
  Type = 0
FEATURE [Sketcher::SketchObject] Sketch107
  ArcFitTolerance = 1e-06
  AttachmentSupport = -> [DatumPlane019]
  ExternalGeometry = -> [Pad032]
  FullyConstrained = true
  MakeInternals = false
  MapMode = 5
  Placement = pos=(0,134.966,0) rot=(1,0,0;1.5708rad)
  sketch-geometry (5):
    g0: LineSegment StartX=52.039 StartY=94.504 StartZ=0 EndX=53.3376 EndY=92.726 EndZ=0
    g1: LineSegment StartX=53.3376 StartY=92.726 StartZ=0 EndX=53.3376 EndY=85.4155 EndZ=0
    g2: LineSegment StartX=53.3376 StartY=85.4155 StartZ=0 EndX=0.254 EndY=28.6566 EndZ=0
    g3: LineSegment StartX=0.254 StartY=28.6566 StartZ=0 EndX=0.254 EndY=31.2596 EndZ=0
    g4: LineSegment StartX=52.039 StartY=94.504 StartZ=0 EndX=0.254 EndY=31.2596 EndZ=0
  constraints (11):
    c: Coincident(g0,g-4)
    c: Coincident(g0,g-3)
    c: Coincident(g1,g0)
    c: Coincident(g1,g-5)
    c: Coincident(g2,g1)
    c: PointOnObject(g2,g-5)
    c: Coincident(g3,g2)
    c: Coincident(g3,g-4)
    c: Vertical(g3)
    c: Coincident(g4,g0)
    c: Coincident(g4,g3)
FEATURE [PartDesign::Pad] Pad033
  BaseFeature = -> Pad032
  Direction = (0,-1,2e-16)
  Length = 1.5748
  Length2 = 10
  Placement = pos=(0,-20.6664,0) rot=(0,0.707107,0.707107;3.14159rad)
  Profile = -> Sketch107
  ReferenceAxis = -> Sketch107 [N_Axis]
  Refine = true
  Suppressed = false
  Type = 0
FEATURE [PartDesign::Pad] Pad019
  BaseFeature = -> Pad033
  Direction = (-1,0,2e-16)
  Length = 1.524
  Length2 = 10
  Placement = pos=(0,-20.6664,0) rot=(0,0.707107,0.707107;3.14159rad)
  Profile = -> Sketch049
  ReferenceAxis = -> Sketch049 [N_Axis]
  Refine = true
  Reversed = true
  Suppressed = false
  Type = 0
FEATURE [Sketcher::SketchObject] Sketch101
  ArcFitTolerance = 1e-06
  AttachmentSupport = -> [Pad019]
  ExternalGeometry = -> [Binder015]
  FullyConstrained = true
  MakeInternals = false
  MapMode = 5
  Placement = pos=(0.254,-20.6664,1.2e-15) rot=(0,-1,0;1.5708rad)
  sketch-geometry (4):
    g0: LineSegment StartX=24.6712 StartY=120.828 StartZ=0 EndX=24.6712 EndY=104.371 EndZ=0
    g1: LineSegment StartX=24.6712 StartY=104.371 StartZ=0 EndX=28.4812 EndY=104.371 EndZ=0
    g2: LineSegment StartX=28.4812 StartY=104.371 StartZ=0 EndX=28.4812 EndY=120.828 EndZ=0
    g3: LineSegment StartX=28.4812 StartY=120.828 StartZ=0 EndX=24.6712 EndY=120.828 EndZ=0
  constraints (12):
    c: Coincident(g0,g1)
    c: Coincident(g1,g2)
    c: Coincident(g2,g3)
    c: Coincident(g3,g0)
    c: Vertical(g0)
    c: Vertical(g2)
    c: Horizontal(g1)
    c: Horizontal(g3)
    c: DistanceX(g-3,g2) = 0.2032
    c: DistanceY(g-3,g2) = 0.2032
    c: DistanceY(g1,g-4) = 0.254
    c: DistanceX(g0,g1) = 3.81
FEATURE [PartDesign::Pocket] Pocket038
  BaseFeature = -> Pad019
  Direction = (1,0,4.9e-15)
  Length = 5
  Length2 = 5
  Placement = pos=(0,-20.6664,0) rot=(0,0.707107,0.707107;3.14159rad)
  Profile = -> Sketch101
  ReferenceAxis = -> Sketch101 [N_Axis]
  Refine = true
  Suppressed = false
  Type = 1
FEATURE [Sketcher::SketchObject] Sketch110
  ArcFitTolerance = 1e-06
  AttachmentSupport = -> [Pocket038]
  ExternalGeometry = -> [Pocket038]
  FullyConstrained = true
  MakeInternals = false
  MapMode = 5
  Placement = pos=(-15.1706,-20.6664,12.4218) rot=(0,-1,0;0.884692rad)
  sketch-geometry (4):
    g0: LineSegment StartX=35.3898 StartY=152.788 StartZ=0 EndX=35.3898 EndY=2.54 EndZ=0
    g1: LineSegment StartX=35.3898 StartY=2.54 StartZ=0 EndX=37.4218 EndY=2.54 EndZ=0
    g2: LineSegment StartX=37.4218 StartY=2.54 StartZ=0 EndX=37.4218 EndY=152.788 EndZ=0
    g3: LineSegment StartX=37.4218 StartY=152.788 StartZ=0 EndX=35.3898 EndY=152.788 EndZ=0
  constraints (12):
    c: Coincident(g0,g1)
    c: Coincident(g1,g2)
    c: Coincident(g2,g3)
    c: Coincident(g3,g0)
    c: Vertical(g0)
    c: Vertical(g2)
    c: Horizontal(g1)
    c: Horizontal(g3)
    c: Horizontal(g2,g-3)
    c: Horizontal(g1,g-4)
    c: Distance(g1,g1) = 2.032
    c: DistanceX(g1,g-4) = -12.7
FEATURE [PartDesign::Pad] Pad036
  BaseFeature = -> Pocket038
  Direction = (-0.77372,0,0.633528)
  Length = 5.08
  Length2 = 10
  Placement = pos=(0,-20.6664,0) rot=(0,0.707107,0.707107;3.14159rad)
  Profile = -> Sketch110
  ReferenceAxis = -> Sketch110 [N_Axis]
  Refine = true
  Reversed = true
  Suppressed = false
  Type = 0
FEATURE [PartDesign::Body] Body003
  AllowCompound = false
  Group = -> [Binder010,Binder011,DatumPlane018,DatumPlane019,Sketch048,Pad018,DatumPlane020,Sketch049,Sketch106,Pad032,Sketch107,Pad033,Sketch110,Pad019,Binder015,Sketch101,Pocket038,Pad036]
  Origin = -> Origin007
  Tip = -> Pad036
